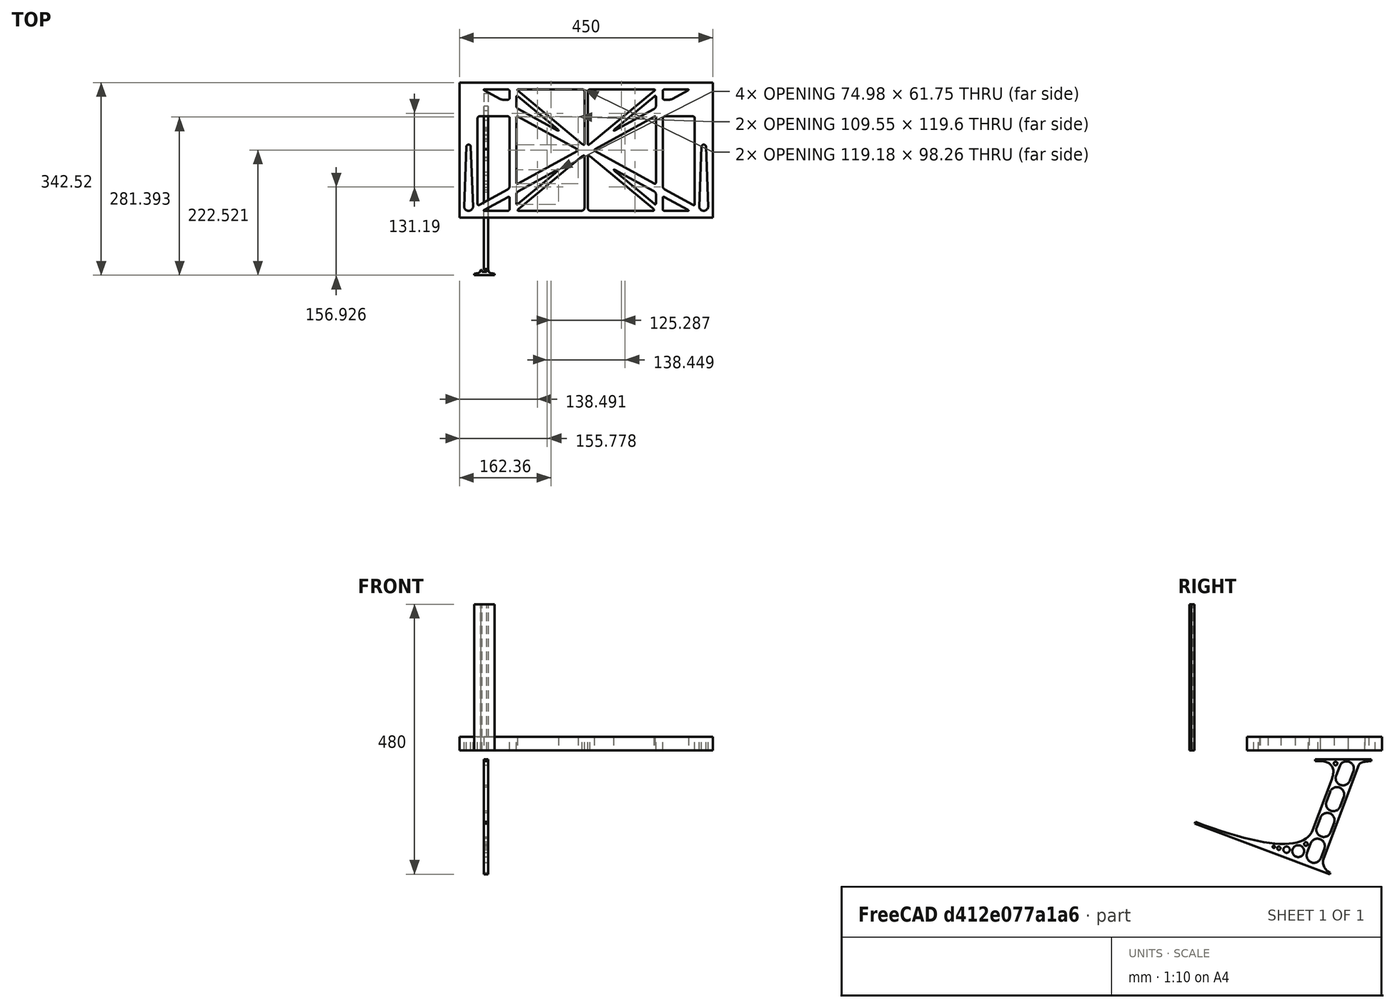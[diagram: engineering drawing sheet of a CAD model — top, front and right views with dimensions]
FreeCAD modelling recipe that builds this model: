
FCSTD DOCUMENT  (FreeCAD 0.19R0.19.2)
Label: laptopStand168FCStd
License: All rights reserved
LicenseURL: http://en.wikipedia.org/wiki/All_rights_reserved
objects: Sketcher::SketchObject×4, Part::Extrusion×3
note: 7 computed .brp shape members not serialized (recipe doc carries the construction recipe); baked Part::Feature solids carry a one-line shape summary decoded from their .brp

FEATURE [Sketcher::SketchObject] Sketch
  FullyConstrained = false
  sketch-geometry (349):
    g0: LineSegment StartX=-10.9272 StartY=-82.7794 StartZ=0 EndX=46.0728 EndY=-51.4823 EndZ=0
    g1: LineSegment StartX=-10.9272 StartY=76.4095 StartZ=0 EndX=-10.9272 EndY=-82.7794 EndZ=0
    g2: LineSegment StartX=46.0728 StartY=76.4095 StartZ=0 EndX=46.0728 EndY=-51.4823 EndZ=0
    g3: LineSegment StartX=-42.9272 StartY=136.221 StartZ=0 EndX=-42.9272 EndY=-103.779 EndZ=0
    g4: LineSegment StartX=407.073 StartY=136.221 StartZ=0 EndX=407.073 EndY=-103.779 EndZ=0
    g5: ArcOfCircle CenterX=-26.9272 CenterY=-83.7794 CenterZ=0 NormalX=0 NormalY=0 NormalZ=1 AngleXU=0 Radius=8 StartAngle=3.14159 EndAngle=6.28319
    g6: ArcOfCircle CenterX=391.073 CenterY=22.1087 CenterZ=0 NormalX=0 NormalY=0 NormalZ=1 AngleXU=0 Radius=8 StartAngle=-4.4e-15 EndAngle=3.14159
    g7: LineSegment StartX=399.073 StartY=22.1087 StartZ=0 EndX=399.073 EndY=-83.7794 EndZ=0
    g8: LineSegment StartX=383.073 StartY=22.1087 StartZ=0 EndX=383.073 EndY=-83.7794 EndZ=0
    g9: ArcOfCircle CenterX=391.073 CenterY=-83.7794 CenterZ=0 NormalX=0 NormalY=0 NormalZ=1 AngleXU=0 Radius=8 StartAngle=3.14159 EndAngle=6.28319
    g10: Circle CenterX=175.022 CenterY=27.0628 CenterZ=0 NormalX=0 NormalY=0 NormalZ=1 AngleXU=0 Radius=1
    g11: Circle CenterX=179.022 CenterY=24.8665 CenterZ=0 NormalX=0 NormalY=0 NormalZ=1 AngleXU=0 Radius=1
    g12: Circle CenterX=179.022 CenterY=27.0628 CenterZ=0 NormalX=0 NormalY=0 NormalZ=1 AngleXU=0 Radius=1
    g13: BSplineCurve PolesCount=3 KnotsCount=2 Degree=2 IsPeriodic=0
    g14: GeomPoint X=175.022 Y=27.0628 Z=0
    g15: GeomPoint X=179.022 Y=27.0628 Z=0
    g16: Circle CenterX=189.124 CenterY=27.0628 CenterZ=0 NormalX=0 NormalY=0 NormalZ=1 AngleXU=0 Radius=1
    g17: Circle CenterX=185.124 CenterY=24.8665 CenterZ=0 NormalX=0 NormalY=0 NormalZ=1 AngleXU=0 Radius=1
    g18: Circle CenterX=185.124 CenterY=27.0628 CenterZ=0 NormalX=0 NormalY=0 NormalZ=1 AngleXU=0 Radius=1
    g19: BSplineCurve PolesCount=3 KnotsCount=2 Degree=2 IsPeriodic=0
    g20: GeomPoint X=189.124 Y=27.0628 Z=0
    g21: GeomPoint X=185.124 Y=27.0628 Z=0
    g22: Circle CenterX=175.022 CenterY=5.37834 CenterZ=0 NormalX=0 NormalY=0 NormalZ=1 AngleXU=0 Radius=1
    g23: Circle CenterX=179.022 CenterY=7.57463 CenterZ=0 NormalX=0 NormalY=0 NormalZ=1 AngleXU=0 Radius=1
    g24: Circle CenterX=179.022 CenterY=5.34704 CenterZ=0 NormalX=0 NormalY=0 NormalZ=1 AngleXU=0 Radius=1
    g25: BSplineCurve PolesCount=3 KnotsCount=2 Degree=2 IsPeriodic=0
    g26: GeomPoint X=175.022 Y=5.37834 Z=0
    g27: GeomPoint X=179.022 Y=5.34704 Z=0
    g28: Circle CenterX=189.124 CenterY=5.37834 CenterZ=0 NormalX=0 NormalY=0 NormalZ=1 AngleXU=0 Radius=1
    g29: Circle CenterX=185.124 CenterY=7.57463 CenterZ=0 NormalX=0 NormalY=0 NormalZ=1 AngleXU=0 Radius=1
    g30: Circle CenterX=185.124 CenterY=5.34704 CenterZ=0 NormalX=0 NormalY=0 NormalZ=1 AngleXU=0 Radius=1
    g31: BSplineCurve PolesCount=3 KnotsCount=2 Degree=2 IsPeriodic=0
    g32: GeomPoint X=189.124 Y=5.37834 Z=0
    g33: GeomPoint X=185.124 Y=5.34704 Z=0
    g34: Circle CenterX=165.871 CenterY=18.1458 CenterZ=0 NormalX=0 NormalY=0 NormalZ=1 AngleXU=0 Radius=1
    g35: Circle CenterX=169.377 CenterY=16.2206 CenterZ=0 NormalX=0 NormalY=0 NormalZ=1 AngleXU=0 Radius=1
    g36: Circle CenterX=165.871 CenterY=14.2954 CenterZ=0 NormalX=0 NormalY=0 NormalZ=1 AngleXU=0 Radius=1
    g37: BSplineCurve PolesCount=3 KnotsCount=2 Degree=2 IsPeriodic=0
    g38: GeomPoint X=165.871 Y=18.1458 Z=0
    g39: GeomPoint X=165.871 Y=14.2954 Z=0
    g40: Circle CenterX=198.275 CenterY=18.1458 CenterZ=0 NormalX=0 NormalY=0 NormalZ=1 AngleXU=0 Radius=1
    g41: Circle CenterX=194.768 CenterY=16.2206 CenterZ=0 NormalX=0 NormalY=0 NormalZ=1 AngleXU=0 Radius=1
    g42: Circle CenterX=198.275 CenterY=14.2954 CenterZ=0 NormalX=0 NormalY=0 NormalZ=1 AngleXU=0 Radius=1
    g43: BSplineCurve PolesCount=3 KnotsCount=2 Degree=2 IsPeriodic=0
    g44: GeomPoint X=198.275 Y=18.1458 Z=0
    g45: GeomPoint X=198.275 Y=14.2954 Z=0
    g46: LineSegment StartX=407.073 StartY=-103.779 StartZ=0 EndX=-42.9272 EndY=-103.779 EndZ=0
    g47: LineSegment StartX=407.073 StartY=136.221 StartZ=0 EndX=-42.9272 EndY=136.221 EndZ=0
    g48: LineSegment StartX=46.0728 StartY=76.4095 StartZ=0 EndX=-10.9272 EndY=76.4095 EndZ=0
    g49: Circle CenterX=125.607 CenterY=54.1951 CenterZ=0 NormalX=0 NormalY=0 NormalZ=1 AngleXU=0 Radius=1
    g50: Circle CenterX=139.632 CenterY=46.4944 CenterZ=0 NormalX=0 NormalY=0 NormalZ=1 AngleXU=0 Radius=1
    g51: Circle CenterX=127.326 CenterY=56.7187 CenterZ=0 NormalX=0 NormalY=0 NormalZ=1 AngleXU=0 Radius=1
    g52: BSplineCurve PolesCount=3 KnotsCount=2 Degree=2 IsPeriodic=0
    g53: GeomPoint X=125.607 Y=54.1951 Z=0
    g54: GeomPoint X=127.326 Y=56.7187 Z=0
    g55: Circle CenterX=236.821 CenterY=56.7187 CenterZ=0 NormalX=0 NormalY=0 NormalZ=1 AngleXU=0 Radius=1
    g56: Circle CenterX=224.513 CenterY=46.4944 CenterZ=0 NormalX=0 NormalY=0 NormalZ=1 AngleXU=0 Radius=1
    g57: Circle CenterX=238.538 CenterY=54.1951 CenterZ=0 NormalX=0 NormalY=0 NormalZ=1 AngleXU=0 Radius=1
    g58: BSplineCurve PolesCount=3 KnotsCount=2 Degree=2 IsPeriodic=0
    g59: GeomPoint X=236.821 Y=56.7187 Z=0
    g60: GeomPoint X=238.538 Y=54.1951 Z=0
    g61: Circle CenterX=238.538 CenterY=-21.7539 CenterZ=0 NormalX=0 NormalY=0 NormalZ=1 AngleXU=0 Radius=1
    g62: Circle CenterX=224.513 CenterY=-14.0532 CenterZ=0 NormalX=0 NormalY=0 NormalZ=1 AngleXU=0 Radius=1
    g63: Circle CenterX=236.821 CenterY=-24.2775 CenterZ=0 NormalX=0 NormalY=0 NormalZ=1 AngleXU=0 Radius=1
    g64: BSplineCurve PolesCount=3 KnotsCount=2 Degree=2 IsPeriodic=0
    g65: GeomPoint X=238.538 Y=-21.7539 Z=0
    g66: GeomPoint X=236.821 Y=-24.2775 Z=0
    g67: Circle CenterX=125.607 CenterY=-21.7539 CenterZ=0 NormalX=0 NormalY=0 NormalZ=1 AngleXU=0 Radius=1
    g68: Circle CenterX=139.632 CenterY=-14.0532 CenterZ=0 NormalX=0 NormalY=0 NormalZ=1 AngleXU=0 Radius=1
    g69: Circle CenterX=127.325 CenterY=-24.2775 CenterZ=0 NormalX=0 NormalY=0 NormalZ=1 AngleXU=0 Radius=1
    g70: BSplineCurve PolesCount=3 KnotsCount=2 Degree=2 IsPeriodic=0
    g71: GeomPoint X=125.607 Y=-21.7539 Z=0
    g72: GeomPoint X=127.325 Y=-24.2775 Z=0
    g73: Circle CenterX=302.996 CenterY=111.695 CenterZ=0 NormalX=0 NormalY=0 NormalZ=1 AngleXU=0 Radius=1
    g74: Circle CenterX=306.073 CenterY=114.251 CenterZ=0 NormalX=0 NormalY=0 NormalZ=1 AngleXU=0 Radius=1
    g75: Circle CenterX=306.073 CenterY=110.251 CenterZ=0 NormalX=0 NormalY=0 NormalZ=1 AngleXU=0 Radius=1
    g76: BSplineCurve PolesCount=3 KnotsCount=2 Degree=2 IsPeriodic=0
    g77: GeomPoint X=302.996 Y=111.695 Z=0
    g78: GeomPoint X=306.073 Y=110.251 Z=0
    g79: Circle CenterX=306.073 CenterY=95.2763 CenterZ=0 NormalX=0 NormalY=0 NormalZ=1 AngleXU=0 Radius=1
    g80: Circle CenterX=306.073 CenterY=91.2763 CenterZ=0 NormalX=0 NormalY=0 NormalZ=1 AngleXU=0 Radius=1
    g81: Circle CenterX=302.567 CenterY=89.3511 CenterZ=0 NormalX=0 NormalY=0 NormalZ=1 AngleXU=0 Radius=1
    g82: BSplineCurve PolesCount=3 KnotsCount=2 Degree=2 IsPeriodic=0
    g83: GeomPoint X=306.073 Y=95.2763 Z=0
    g84: GeomPoint X=302.567 Y=89.3511 Z=0
    g85: LineSegment StartX=306.073 StartY=110.251 StartZ=0 EndX=306.073 EndY=95.2763 EndZ=0
    g86: LineSegment StartX=302.996 StartY=111.695 StartZ=0 EndX=236.821 EndY=56.7187 EndZ=0
    g87: LineSegment StartX=238.538 StartY=54.1951 StartZ=0 EndX=302.567 EndY=89.3511 EndZ=0
    g88: Circle CenterX=61.1496 CenterY=111.695 CenterZ=0 NormalX=0 NormalY=0 NormalZ=1 AngleXU=0 Radius=1
    g89: Circle CenterX=58.0728 CenterY=114.251 CenterZ=0 NormalX=0 NormalY=0 NormalZ=1 AngleXU=0 Radius=1
    g90: Circle CenterX=58.0728 CenterY=110.251 CenterZ=0 NormalX=0 NormalY=0 NormalZ=1 AngleXU=0 Radius=1
    g91: BSplineCurve PolesCount=3 KnotsCount=2 Degree=2 IsPeriodic=0
    g92: GeomPoint X=61.1496 Y=111.695 Z=0
    g93: GeomPoint X=58.0728 Y=110.251 Z=0
    g94: Circle CenterX=61.5791 CenterY=89.3511 CenterZ=0 NormalX=0 NormalY=0 NormalZ=1 AngleXU=0 Radius=1
    g95: Circle CenterX=58.0728 CenterY=91.2763 CenterZ=0 NormalX=0 NormalY=0 NormalZ=1 AngleXU=0 Radius=1
    g96: Circle CenterX=58.0728 CenterY=95.2763 CenterZ=0 NormalX=0 NormalY=0 NormalZ=1 AngleXU=0 Radius=1
    g97: BSplineCurve PolesCount=3 KnotsCount=2 Degree=2 IsPeriodic=0
    g98: GeomPoint X=61.5791 Y=89.3511 Z=0
    g99: GeomPoint X=58.0728 Y=95.2763 Z=0
    g100: LineSegment StartX=58.0728 StartY=110.251 StartZ=0 EndX=58.0728 EndY=95.2763 EndZ=0
    g101: LineSegment StartX=61.1496 StartY=111.695 StartZ=0 EndX=127.326 EndY=56.7187 EndZ=0
    g102: LineSegment StartX=125.607 StartY=54.1951 StartZ=0 EndX=61.5791 EndY=89.3511 EndZ=0
    g103: Circle CenterX=61.5791 CenterY=-56.9099 CenterZ=0 NormalX=0 NormalY=0 NormalZ=1 AngleXU=0 Radius=1
    g104: Circle CenterX=58.0728 CenterY=-58.8351 CenterZ=0 NormalX=0 NormalY=0 NormalZ=1 AngleXU=0 Radius=1
    g105: Circle CenterX=58.0728 CenterY=-62.8351 CenterZ=0 NormalX=0 NormalY=0 NormalZ=1 AngleXU=0 Radius=1
    g106: BSplineCurve PolesCount=3 KnotsCount=2 Degree=2 IsPeriodic=0
    g107: GeomPoint X=61.5791 Y=-56.9099 Z=0
    g108: GeomPoint X=58.0728 Y=-62.8351 Z=0
    g109: Circle CenterX=58.0728 CenterY=-77.8102 CenterZ=0 NormalX=0 NormalY=0 NormalZ=1 AngleXU=0 Radius=1
    g110: Circle CenterX=58.0728 CenterY=-81.8102 CenterZ=0 NormalX=0 NormalY=0 NormalZ=1 AngleXU=0 Radius=1
    g111: Circle CenterX=61.1496 CenterY=-79.2541 CenterZ=0 NormalX=0 NormalY=0 NormalZ=1 AngleXU=0 Radius=1
    g112: BSplineCurve PolesCount=3 KnotsCount=2 Degree=2 IsPeriodic=0
    g113: GeomPoint X=58.0728 Y=-77.8102 Z=0
    g114: GeomPoint X=61.1496 Y=-79.2541 Z=0
    g115: LineSegment StartX=58.0728 StartY=-62.8351 StartZ=0 EndX=58.0728 EndY=-77.8102 EndZ=0
    g116: LineSegment StartX=61.1496 StartY=-79.2541 StartZ=0 EndX=127.325 EndY=-24.2775 EndZ=0
    g117: LineSegment StartX=125.607 StartY=-21.7539 StartZ=0 EndX=61.5791 EndY=-56.9099 EndZ=0
    g118: Circle CenterX=302.567 CenterY=-56.9099 CenterZ=0 NormalX=0 NormalY=0 NormalZ=1 AngleXU=0 Radius=1
    g119: Circle CenterX=306.073 CenterY=-58.8351 CenterZ=0 NormalX=0 NormalY=0 NormalZ=1 AngleXU=0 Radius=1
    g120: Circle CenterX=306.073 CenterY=-62.8351 CenterZ=0 NormalX=0 NormalY=0 NormalZ=1 AngleXU=0 Radius=1
    g121: BSplineCurve PolesCount=3 KnotsCount=2 Degree=2 IsPeriodic=0
    g122: GeomPoint X=302.567 Y=-56.9099 Z=0
    g123: GeomPoint X=306.073 Y=-62.8351 Z=0
    g124: Circle CenterX=302.996 CenterY=-79.2541 CenterZ=0 NormalX=0 NormalY=0 NormalZ=1 AngleXU=0 Radius=1
    g125: Circle CenterX=306.073 CenterY=-81.8102 CenterZ=0 NormalX=0 NormalY=0 NormalZ=1 AngleXU=0 Radius=1
    g126: Circle CenterX=306.073 CenterY=-77.8102 CenterZ=0 NormalX=0 NormalY=0 NormalZ=1 AngleXU=0 Radius=1
    g127: BSplineCurve PolesCount=3 KnotsCount=2 Degree=2 IsPeriodic=0
    g128: GeomPoint X=302.996 Y=-79.2541 Z=0
    g129: GeomPoint X=306.073 Y=-77.8102 Z=0
    g130: LineSegment StartX=306.073 StartY=-62.8351 StartZ=0 EndX=306.073 EndY=-77.8102 EndZ=0
    g131: LineSegment StartX=302.996 StartY=-79.2541 StartZ=0 EndX=236.821 EndY=-24.2775 EndZ=0
    g132: LineSegment StartX=238.538 StartY=-21.7539 StartZ=0 EndX=302.567 EndY=-56.9099 EndZ=0
    g133: Circle CenterX=61.6457 CenterY=-88.8112 CenterZ=0 NormalX=0 NormalY=0 NormalZ=1 AngleXU=0 Radius=1
    g134: Circle CenterX=58.0728 CenterY=-91.7794 CenterZ=0 NormalX=0 NormalY=0 NormalZ=1 AngleXU=0 Radius=1
    g135: Circle CenterX=63.9135 CenterY=-91.7794 CenterZ=0 NormalX=0 NormalY=0 NormalZ=1 AngleXU=0 Radius=1
    g136: BSplineCurve PolesCount=3 KnotsCount=2 Degree=2 IsPeriodic=0
    g137: GeomPoint X=61.6457 Y=-88.8112 Z=0
    g138: GeomPoint X=63.9135 Y=-91.7794 Z=0
    g139: Circle CenterX=179.022 CenterY=-85.8163 CenterZ=0 NormalX=0 NormalY=0 NormalZ=1 AngleXU=0 Radius=1
    g140: Circle CenterX=179.022 CenterY=-91.7794 CenterZ=0 NormalX=0 NormalY=0 NormalZ=1 AngleXU=0 Radius=1
    g141: Circle CenterX=171.895 CenterY=-91.7794 CenterZ=0 NormalX=0 NormalY=0 NormalZ=1 AngleXU=0 Radius=1
    g142: BSplineCurve PolesCount=3 KnotsCount=2 Degree=2 IsPeriodic=0
    g143: GeomPoint X=179.022 Y=-85.8163 Z=0
    g144: GeomPoint X=171.895 Y=-91.7794 Z=0
    g145: Circle CenterX=185.124 CenterY=-86.2028 CenterZ=0 NormalX=0 NormalY=0 NormalZ=1 AngleXU=0 Radius=1
    g146: Circle CenterX=185.124 CenterY=-91.7794 CenterZ=0 NormalX=0 NormalY=0 NormalZ=1 AngleXU=0 Radius=1
    g147: Circle CenterX=191.747 CenterY=-91.7794 CenterZ=0 NormalX=0 NormalY=0 NormalZ=1 AngleXU=0 Radius=1
    g148: BSplineCurve PolesCount=3 KnotsCount=2 Degree=2 IsPeriodic=0
    g149: GeomPoint X=185.124 Y=-86.2028 Z=0
    g150: GeomPoint X=191.747 Y=-91.7794 Z=0
    g151: Circle CenterX=299.888 CenterY=-86.6413 CenterZ=0 NormalX=0 NormalY=0 NormalZ=1 AngleXU=0 Radius=1
    g152: Circle CenterX=306.073 CenterY=-91.7794 CenterZ=0 NormalX=0 NormalY=0 NormalZ=1 AngleXU=0 Radius=1
    g153: Circle CenterX=298.776 CenterY=-91.7794 CenterZ=0 NormalX=0 NormalY=0 NormalZ=1 AngleXU=0 Radius=1
    g154: BSplineCurve PolesCount=3 KnotsCount=2 Degree=2 IsPeriodic=0
    g155: GeomPoint X=299.888 Y=-86.6413 Z=0
    g156: GeomPoint X=298.776 Y=-91.7794 Z=0
    g157: LineSegment StartX=189.124 StartY=5.37834 StartZ=0 EndX=299.888 EndY=-86.6413 EndZ=0
    g158: LineSegment StartX=298.776 StartY=-91.7794 StartZ=0 EndX=191.747 EndY=-91.7794 EndZ=0
    g159: LineSegment StartX=185.124 StartY=-86.2028 StartZ=0 EndX=185.124 EndY=5.34704 EndZ=0
    g160: LineSegment StartX=179.022 StartY=5.34704 StartZ=0 EndX=179.022 EndY=-85.8163 EndZ=0
    g161: LineSegment StartX=171.895 StartY=-91.7794 StartZ=0 EndX=63.9135 EndY=-91.7794 EndZ=0
    g162: LineSegment StartX=61.6457 StartY=-88.8112 StartZ=0 EndX=175.022 EndY=5.37834 EndZ=0
    g163: Circle CenterX=302.073 CenterY=124.221 CenterZ=0 NormalX=0 NormalY=0 NormalZ=1 AngleXU=0 Radius=1
    g164: Circle CenterX=306.073 CenterY=124.221 CenterZ=0 NormalX=0 NormalY=0 NormalZ=1 AngleXU=0 Radius=1
    g165: Circle CenterX=302.996 CenterY=121.665 CenterZ=0 NormalX=0 NormalY=0 NormalZ=1 AngleXU=0 Radius=1
    g166: BSplineCurve PolesCount=3 KnotsCount=2 Degree=2 IsPeriodic=0
    g167: GeomPoint X=302.073 Y=124.221 Z=0
    g168: GeomPoint X=302.996 Y=121.665 Z=0
    g169: Circle CenterX=189.124 CenterY=124.221 CenterZ=0 NormalX=0 NormalY=0 NormalZ=1 AngleXU=0 Radius=1
    g170: Circle CenterX=185.124 CenterY=124.221 CenterZ=0 NormalX=0 NormalY=0 NormalZ=1 AngleXU=0 Radius=1
    g171: Circle CenterX=185.124 CenterY=120.221 CenterZ=0 NormalX=0 NormalY=0 NormalZ=1 AngleXU=0 Radius=1
    g172: BSplineCurve PolesCount=3 KnotsCount=2 Degree=2 IsPeriodic=0
    g173: GeomPoint X=189.124 Y=124.221 Z=0
    g174: GeomPoint X=185.124 Y=120.221 Z=0
    g175: Circle CenterX=175.022 CenterY=124.221 CenterZ=0 NormalX=0 NormalY=0 NormalZ=1 AngleXU=0 Radius=1
    g176: Circle CenterX=179.022 CenterY=124.221 CenterZ=0 NormalX=0 NormalY=0 NormalZ=1 AngleXU=0 Radius=1
    g177: Circle CenterX=179.022 CenterY=120.221 CenterZ=0 NormalX=0 NormalY=0 NormalZ=1 AngleXU=0 Radius=1
    g178: BSplineCurve PolesCount=3 KnotsCount=2 Degree=2 IsPeriodic=0
    g179: GeomPoint X=175.022 Y=124.221 Z=0
    g180: GeomPoint X=179.022 Y=120.221 Z=0
    g181: Circle CenterX=62.0728 CenterY=124.221 CenterZ=0 NormalX=0 NormalY=0 NormalZ=1 AngleXU=0 Radius=1
    g182: Circle CenterX=58.0728 CenterY=124.221 CenterZ=0 NormalX=0 NormalY=0 NormalZ=1 AngleXU=0 Radius=1
    g183: Circle CenterX=61.1496 CenterY=121.665 CenterZ=0 NormalX=0 NormalY=0 NormalZ=1 AngleXU=0 Radius=1
    g184: BSplineCurve PolesCount=3 KnotsCount=2 Degree=2 IsPeriodic=0
    g185: GeomPoint X=62.0728 Y=124.221 Z=0
    g186: GeomPoint X=61.1496 Y=121.665 Z=0
    g187: LineSegment StartX=62.0728 StartY=124.221 StartZ=0 EndX=175.022 EndY=124.221 EndZ=0
    g188: LineSegment StartX=179.022 StartY=120.221 StartZ=0 EndX=179.022 EndY=27.0628 EndZ=0
    g189: LineSegment StartX=185.124 StartY=27.0628 StartZ=0 EndX=185.124 EndY=120.221 EndZ=0
    g190: LineSegment StartX=189.124 StartY=124.221 StartZ=0 EndX=302.073 EndY=124.221 EndZ=0
    g191: LineSegment StartX=302.996 StartY=121.665 StartZ=0 EndX=189.124 EndY=27.0628 EndZ=0
    g192: LineSegment StartX=175.022 StartY=27.0628 StartZ=0 EndX=61.1496 EndY=121.665 EndZ=0
    g193: Circle CenterX=61.5791 CenterY=75.4095 CenterZ=0 NormalX=0 NormalY=0 NormalZ=1 AngleXU=0 Radius=1
    g194: Circle CenterX=58.0728 CenterY=77.3346 CenterZ=0 NormalX=0 NormalY=0 NormalZ=1 AngleXU=0 Radius=1
    g195: Circle CenterX=58.0728 CenterY=73.3346 CenterZ=0 NormalX=0 NormalY=0 NormalZ=1 AngleXU=0 Radius=1
    g196: BSplineCurve PolesCount=3 KnotsCount=2 Degree=2 IsPeriodic=0
    g197: GeomPoint X=61.5791 Y=75.4095 Z=0
    g198: GeomPoint X=58.0728 Y=73.3346 Z=0
    g199: Circle CenterX=58.0728 CenterY=-40.8935 CenterZ=0 NormalX=0 NormalY=0 NormalZ=1 AngleXU=0 Radius=1
    g200: Circle CenterX=58.0728 CenterY=-44.8935 CenterZ=0 NormalX=0 NormalY=0 NormalZ=1 AngleXU=0 Radius=1
    g201: Circle CenterX=61.5791 CenterY=-42.9683 CenterZ=0 NormalX=0 NormalY=0 NormalZ=1 AngleXU=0 Radius=1
    g202: BSplineCurve PolesCount=3 KnotsCount=2 Degree=2 IsPeriodic=0
    g203: GeomPoint X=58.0728 Y=-40.8935 Z=0
    g204: GeomPoint X=61.5791 Y=-42.9683 Z=0
    g205: LineSegment StartX=61.5791 StartY=-42.9683 StartZ=0 EndX=165.871 EndY=14.2954 EndZ=0
    g206: LineSegment StartX=165.871 StartY=18.1458 StartZ=0 EndX=61.5791 EndY=75.4095 EndZ=0
    g207: LineSegment StartX=58.0728 StartY=73.3346 StartZ=0 EndX=58.0728 EndY=-40.8935 EndZ=0
    g208: Circle CenterX=302.567 CenterY=-42.9683 CenterZ=0 NormalX=0 NormalY=0 NormalZ=1 AngleXU=0 Radius=1
    g209: Circle CenterX=306.073 CenterY=-44.8935 CenterZ=0 NormalX=0 NormalY=0 NormalZ=1 AngleXU=0 Radius=1
    g210: Circle CenterX=306.073 CenterY=-40.8935 CenterZ=0 NormalX=0 NormalY=0 NormalZ=1 AngleXU=0 Radius=1
    g211: BSplineCurve PolesCount=3 KnotsCount=2 Degree=2 IsPeriodic=0
    g212: GeomPoint X=302.567 Y=-42.9683 Z=0
    g213: GeomPoint X=306.073 Y=-40.8935 Z=0
    g214: Circle CenterX=306.073 CenterY=73.3346 CenterZ=0 NormalX=0 NormalY=0 NormalZ=1 AngleXU=0 Radius=1
    g215: Circle CenterX=306.073 CenterY=77.3346 CenterZ=0 NormalX=0 NormalY=0 NormalZ=1 AngleXU=0 Radius=1
    g216: Circle CenterX=302.567 CenterY=75.4095 CenterZ=0 NormalX=0 NormalY=0 NormalZ=1 AngleXU=0 Radius=1
    g217: BSplineCurve PolesCount=3 KnotsCount=2 Degree=2 IsPeriodic=0
    g218: GeomPoint X=306.073 Y=73.3346 Z=0
    g219: GeomPoint X=302.567 Y=75.4095 Z=0
    g220: LineSegment StartX=302.567 StartY=-42.9683 StartZ=0 EndX=198.275 EndY=14.2954 EndZ=0
    g221: LineSegment StartX=198.275 StartY=18.1458 StartZ=0 EndX=302.567 EndY=75.4095 EndZ=0
    g222: LineSegment StartX=306.073 StartY=73.3346 StartZ=0 EndX=306.073 EndY=-40.8935 EndZ=0
    g223: LineSegment StartX=322.073 StartY=105.865 StartZ=0 EndX=328.643 EndY=105.865 EndZ=0
    g224: LineSegment StartX=318.073 StartY=120.221 StartZ=0 EndX=318.073 EndY=109.865 EndZ=0
    g225: LineSegment StartX=336.157 StartY=107.779 StartZ=0 EndX=362.567 EndY=122.294 EndZ=0
    g226: Circle CenterX=362.073 CenterY=124.221 CenterZ=0 NormalX=0 NormalY=0 NormalZ=1 AngleXU=0 Radius=1
    g227: Circle CenterX=366.073 CenterY=124.221 CenterZ=0 NormalX=0 NormalY=0 NormalZ=1 AngleXU=0 Radius=1
    g228: Circle CenterX=362.567 CenterY=122.294 CenterZ=0 NormalX=0 NormalY=0 NormalZ=1 AngleXU=0 Radius=1
    g229: BSplineCurve PolesCount=3 KnotsCount=2 Degree=2 IsPeriodic=0
    g230: GeomPoint X=362.073 Y=124.221 Z=0
    g231: GeomPoint X=362.567 Y=122.294 Z=0
    g232: Circle CenterX=322.073 CenterY=124.221 CenterZ=0 NormalX=0 NormalY=0 NormalZ=1 AngleXU=0 Radius=1
    g233: Circle CenterX=318.073 CenterY=124.221 CenterZ=0 NormalX=0 NormalY=0 NormalZ=1 AngleXU=0 Radius=1
    g234: Circle CenterX=318.073 CenterY=120.221 CenterZ=0 NormalX=0 NormalY=0 NormalZ=1 AngleXU=0 Radius=1
    g235: BSplineCurve PolesCount=3 KnotsCount=2 Degree=2 IsPeriodic=0
    g236: GeomPoint X=322.073 Y=124.221 Z=0
    g237: GeomPoint X=318.073 Y=120.221 Z=0
    g238: Circle CenterX=322.073 CenterY=105.865 CenterZ=0 NormalX=0 NormalY=0 NormalZ=1 AngleXU=0 Radius=1
    g239: Circle CenterX=318.073 CenterY=105.865 CenterZ=0 NormalX=0 NormalY=0 NormalZ=1 AngleXU=0 Radius=1
    g240: Circle CenterX=318.073 CenterY=109.865 CenterZ=0 NormalX=0 NormalY=0 NormalZ=1 AngleXU=0 Radius=1
    g241: BSplineCurve PolesCount=3 KnotsCount=2 Degree=2 IsPeriodic=0
    g242: GeomPoint X=322.073 Y=105.865 Z=0
    g243: GeomPoint X=318.073 Y=109.865 Z=0
    g244: Circle CenterX=336.157 CenterY=107.779 CenterZ=0 NormalX=0 NormalY=0 NormalZ=1 AngleXU=0 Radius=1
    g245: Circle CenterX=332.651 CenterY=105.853 CenterZ=0 NormalX=0 NormalY=0 NormalZ=1 AngleXU=0 Radius=1
    g246: Circle CenterX=328.643 CenterY=105.865 CenterZ=0 NormalX=0 NormalY=0 NormalZ=1 AngleXU=0 Radius=1
    g247: BSplineCurve PolesCount=3 KnotsCount=2 Degree=2 IsPeriodic=0
    g248: GeomPoint X=336.157 Y=107.779 Z=0
    g249: GeomPoint X=328.643 Y=105.865 Z=0
    g250: LineSegment StartX=322.073 StartY=124.221 StartZ=0 EndX=362.073 EndY=124.221 EndZ=0
    g251: Circle CenterX=371.567 CenterY=-80.8644 CenterZ=0 NormalX=0 NormalY=0 NormalZ=1 AngleXU=0 Radius=1
    g252: Circle CenterX=375.073 CenterY=-82.7896 CenterZ=0 NormalX=0 NormalY=0 NormalZ=1 AngleXU=0 Radius=1
    g253: Circle CenterX=375.073 CenterY=-78.7896 CenterZ=0 NormalX=0 NormalY=0 NormalZ=1 AngleXU=0 Radius=1
    g254: BSplineCurve PolesCount=3 KnotsCount=2 Degree=2 IsPeriodic=0
    g255: GeomPoint X=371.567 Y=-80.8644 Z=0
    g256: GeomPoint X=375.073 Y=-78.7896 Z=0
    g257: Circle CenterX=321.579 CenterY=-53.4075 CenterZ=0 NormalX=0 NormalY=0 NormalZ=1 AngleXU=0 Radius=1
    g258: Circle CenterX=318.073 CenterY=-51.4823 CenterZ=0 NormalX=0 NormalY=0 NormalZ=1 AngleXU=0 Radius=1
    g259: Circle CenterX=318.073 CenterY=-47.4805 CenterZ=0 NormalX=0 NormalY=0 NormalZ=1 AngleXU=0 Radius=1
    g260: BSplineCurve PolesCount=3 KnotsCount=2 Degree=2 IsPeriodic=0
    g261: GeomPoint X=321.579 Y=-53.4075 Z=0
    g262: GeomPoint X=318.073 Y=-47.4805 Z=0
    g263: LineSegment StartX=371.567 StartY=-80.8644 StartZ=0 EndX=321.579 EndY=-53.4075 EndZ=0
    g264: Circle CenterX=321.579 CenterY=-67.3492 CenterZ=0 NormalX=0 NormalY=0 NormalZ=1 AngleXU=0 Radius=1
    g265: Circle CenterX=318.073 CenterY=-65.424 CenterZ=0 NormalX=0 NormalY=0 NormalZ=1 AngleXU=0 Radius=1
    g266: Circle CenterX=318.073 CenterY=-69.424 CenterZ=0 NormalX=0 NormalY=0 NormalZ=1 AngleXU=0 Radius=1
    g267: BSplineCurve PolesCount=3 KnotsCount=2 Degree=2 IsPeriodic=0
    g268: GeomPoint X=321.579 Y=-67.3492 Z=0
    g269: GeomPoint X=318.073 Y=-69.424 Z=0
    g270: Circle CenterX=362.567 CenterY=-89.8542 CenterZ=0 NormalX=0 NormalY=0 NormalZ=1 AngleXU=0 Radius=1
    g271: Circle CenterX=366.073 CenterY=-91.7794 CenterZ=0 NormalX=0 NormalY=0 NormalZ=1 AngleXU=0 Radius=1
    g272: Circle CenterX=362.073 CenterY=-91.7794 CenterZ=0 NormalX=0 NormalY=0 NormalZ=1 AngleXU=0 Radius=1
    g273: BSplineCurve PolesCount=3 KnotsCount=2 Degree=2 IsPeriodic=0
    g274: GeomPoint X=362.567 Y=-89.8542 Z=0
    g275: GeomPoint X=362.073 Y=-91.7794 Z=0
    g276: Circle CenterX=322.073 CenterY=-91.7794 CenterZ=0 NormalX=0 NormalY=0 NormalZ=1 AngleXU=0 Radius=1
    g277: Circle CenterX=318.073 CenterY=-91.7794 CenterZ=0 NormalX=0 NormalY=0 NormalZ=1 AngleXU=0 Radius=1
    g278: Circle CenterX=318.073 CenterY=-87.7794 CenterZ=0 NormalX=0 NormalY=0 NormalZ=1 AngleXU=0 Radius=1
    g279: BSplineCurve PolesCount=3 KnotsCount=2 Degree=2 IsPeriodic=0
    g280: GeomPoint X=322.073 Y=-91.7794 Z=0
    g281: GeomPoint X=318.073 Y=-87.7794 Z=0
    g282: LineSegment StartX=362.567 StartY=-89.8542 StartZ=0 EndX=321.579 EndY=-67.3492 EndZ=0
    g283: LineSegment StartX=318.073 StartY=-69.424 StartZ=0 EndX=318.073 EndY=-87.7794 EndZ=0
    g284: LineSegment StartX=322.073 StartY=-91.7794 StartZ=0 EndX=362.073 EndY=-91.7794 EndZ=0
    g285: Circle CenterX=2.07281 CenterY=124.221 CenterZ=0 NormalX=0 NormalY=0 NormalZ=1 AngleXU=0 Radius=1
    g286: Circle CenterX=1.57905 CenterY=122.295 CenterZ=0 NormalX=0 NormalY=0 NormalZ=1 AngleXU=0 Radius=1
    g287: BSplineCurve PolesCount=3 KnotsCount=2 Degree=2 IsPeriodic=0
    g288: GeomPoint X=2.07281 Y=124.221 Z=0
    g289: GeomPoint X=1.57905 Y=122.295 Z=0
    g290: Circle CenterX=42.0728 CenterY=124.221 CenterZ=0 NormalX=0 NormalY=0 NormalZ=1 AngleXU=0 Radius=1
    g291: Circle CenterX=46.0728 CenterY=124.221 CenterZ=0 NormalX=0 NormalY=0 NormalZ=1 AngleXU=0 Radius=1
    g292: Circle CenterX=46.0728 CenterY=120.221 CenterZ=0 NormalX=0 NormalY=0 NormalZ=1 AngleXU=0 Radius=1
    g293: BSplineCurve PolesCount=3 KnotsCount=2 Degree=2 IsPeriodic=0
    g294: GeomPoint X=42.0728 Y=124.221 Z=0
    g295: GeomPoint X=46.0728 Y=120.221 Z=0
    g296: Circle CenterX=46.0728 CenterY=109.865 CenterZ=0 NormalX=0 NormalY=0 NormalZ=1 AngleXU=0 Radius=1
    g297: Circle CenterX=46.0728 CenterY=105.865 CenterZ=0 NormalX=0 NormalY=0 NormalZ=1 AngleXU=0 Radius=1
    g298: Circle CenterX=42.0728 CenterY=105.865 CenterZ=0 NormalX=0 NormalY=0 NormalZ=1 AngleXU=0 Radius=1
    g299: BSplineCurve PolesCount=3 KnotsCount=2 Degree=2 IsPeriodic=0
    g300: GeomPoint X=46.0728 Y=109.865 Z=0
    g301: GeomPoint X=42.0728 Y=105.865 Z=0
    g302: Circle CenterX=35.5028 CenterY=105.865 CenterZ=0 NormalX=0 NormalY=0 NormalZ=1 AngleXU=0 Radius=1
    g303: Circle CenterX=31.5028 CenterY=105.865 CenterZ=0 NormalX=0 NormalY=0 NormalZ=1 AngleXU=0 Radius=1
    g304: Circle CenterX=27.9965 CenterY=107.79 CenterZ=0 NormalX=0 NormalY=0 NormalZ=1 AngleXU=0 Radius=1
    g305: BSplineCurve PolesCount=3 KnotsCount=2 Degree=2 IsPeriodic=0
    g306: GeomPoint X=35.5028 Y=105.865 Z=0
    g307: GeomPoint X=27.9965 Y=107.79 Z=0
    g308: LineSegment StartX=2.07281 StartY=124.221 StartZ=0 EndX=42.0728 EndY=124.221 EndZ=0
    g309: LineSegment StartX=46.0728 StartY=120.221 StartZ=0 EndX=46.0728 EndY=109.865 EndZ=0
    g310: LineSegment StartX=42.0728 StartY=105.865 StartZ=0 EndX=35.5028 EndY=105.865 EndZ=0
    g311: LineSegment StartX=27.9965 StartY=107.79 StartZ=0 EndX=1.57905 EndY=122.295 EndZ=0
    g312: Circle CenterX=42.5666 CenterY=-67.3492 CenterZ=0 NormalX=0 NormalY=0 NormalZ=1 AngleXU=0 Radius=1
    g313: Circle CenterX=46.0728 CenterY=-65.424 CenterZ=0 NormalX=0 NormalY=0 NormalZ=1 AngleXU=0 Radius=1
    g314: Circle CenterX=46.0728 CenterY=-69.424 CenterZ=0 NormalX=0 NormalY=0 NormalZ=1 AngleXU=0 Radius=1
    g315: BSplineCurve PolesCount=3 KnotsCount=2 Degree=2 IsPeriodic=0
    g316: GeomPoint X=42.5666 Y=-67.3492 Z=0
    g317: GeomPoint X=46.0728 Y=-69.424 Z=0
    g318: Circle CenterX=46.0728 CenterY=-87.7794 CenterZ=0 NormalX=0 NormalY=0 NormalZ=1 AngleXU=0 Radius=1
    g319: Circle CenterX=46.0728 CenterY=-91.7794 CenterZ=0 NormalX=0 NormalY=0 NormalZ=1 AngleXU=0 Radius=1
    g320: Circle CenterX=42.0728 CenterY=-91.7794 CenterZ=0 NormalX=0 NormalY=0 NormalZ=1 AngleXU=0 Radius=1
    g321: BSplineCurve PolesCount=3 KnotsCount=2 Degree=2 IsPeriodic=0
    g322: GeomPoint X=46.0728 Y=-87.7794 Z=0
    g323: GeomPoint X=42.0728 Y=-91.7794 Z=0
    g324: Circle CenterX=2.07281 CenterY=-91.7794 CenterZ=0 NormalX=0 NormalY=0 NormalZ=1 AngleXU=0 Radius=1
    g325: Circle CenterX=-1.92719 CenterY=-91.7794 CenterZ=0 NormalX=0 NormalY=0 NormalZ=1 AngleXU=0 Radius=1
    g326: Circle CenterX=1.57905 CenterY=-89.8542 CenterZ=0 NormalX=0 NormalY=0 NormalZ=1 AngleXU=0 Radius=1
    g327: BSplineCurve PolesCount=3 KnotsCount=2 Degree=2 IsPeriodic=0
    g328: GeomPoint X=2.07281 Y=-91.7794 Z=0
    g329: GeomPoint X=1.57905 Y=-89.8542 Z=0
    g330: LineSegment StartX=2.07281 StartY=-91.7794 StartZ=0 EndX=42.0728 EndY=-91.7794 EndZ=0
    g331: LineSegment StartX=46.0728 StartY=-87.7794 StartZ=0 EndX=46.0728 EndY=-69.424 EndZ=0
    g332: LineSegment StartX=42.5666 StartY=-67.3492 StartZ=0 EndX=1.57905 EndY=-89.8542 EndZ=0
    g333: Circle CenterX=322.073 CenterY=76.4095 CenterZ=0 NormalX=0 NormalY=0 NormalZ=1 AngleXU=0 Radius=4
    g334: BSplineCurve PolesCount=3 KnotsCount=2 Degree=2 IsPeriodic=0
    g335: GeomPoint X=318.073 Y=72.4095 Z=0
    g336: GeomPoint X=322.073 Y=76.4095 Z=0
    g337: Circle CenterX=375.073 CenterY=72.4095 CenterZ=0 NormalX=0 NormalY=0 NormalZ=1 AngleXU=0 Radius=1
    g338: Circle CenterX=375.073 CenterY=76.4095 CenterZ=0 NormalX=0 NormalY=0 NormalZ=1 AngleXU=0 Radius=1
    g339: Circle CenterX=371.073 CenterY=76.4095 CenterZ=0 NormalX=0 NormalY=0 NormalZ=1 AngleXU=0 Radius=1
    g340: BSplineCurve PolesCount=3 KnotsCount=2 Degree=2 IsPeriodic=0
    g341: GeomPoint X=375.073 Y=72.4095 Z=0
    g342: GeomPoint X=371.073 Y=76.4095 Z=0
    g343: LineSegment StartX=322.073 StartY=76.4095 StartZ=0 EndX=371.073 EndY=76.4095 EndZ=0
    g344: LineSegment StartX=318.073 StartY=72.4095 StartZ=0 EndX=318.073 EndY=-47.4805 EndZ=0
    g345: LineSegment StartX=375.073 StartY=72.4095 StartZ=0 EndX=375.073 EndY=-78.7896 EndZ=0
    g346: ArcOfCircle CenterX=-26.9272 CenterY=22.1087 CenterZ=0 NormalX=0 NormalY=0 NormalZ=1 AngleXU=0 Radius=4 StartAngle=5e-16 EndAngle=3.14159
    g347: LineSegment StartX=-30.9272 StartY=22.1087 StartZ=0 EndX=-34.9272 EndY=-83.7794 EndZ=0
    g348: LineSegment StartX=-18.9272 StartY=-83.7794 StartZ=0 EndX=-22.9272 EndY=22.1087 EndZ=0
  constraints (572):
    c: Coincident(g0,g2)
    c: Block(g0)
    c: Block(g1)
    c: Vertical(g3)
    c: Vertical(g4)
    c: Block(g4)
    c: Block(g3)
    c: Tangent(g6,g7) = 1.5708
    c: Tangent(g7,g9) = 1.5708
    c: Equal(g6,g9)
    c: Coincident(g8,g6)
    c: Coincident(g8,g9)
    c: Block(g7)
    c: Block(g8)
    c: Weight(g10) = 1
    c: Equal(g10,g11)
    c: Equal(g10,g12)
    c: InternalAlignment(g10,g13)
    c: InternalAlignment(g11,g13)
    c: InternalAlignment(g12,g13)
    c: InternalAlignment(g14,g13)
    c: InternalAlignment(g15,g13)
    c: Weight(g16) = 1
    c: Equal(g16,g17)
    c: Equal(g16,g18)
    c: InternalAlignment(g16,g19)
    c: InternalAlignment(g17,g19)
    c: InternalAlignment(g18,g19)
    c: InternalAlignment(g20,g19)
    c: InternalAlignment(g21,g19)
    c: Block(g19)
    c: Block(g13)
    c: Weight(g22) = 1
    c: Equal(g22,g23)
    c: Equal(g22,g24)
    c: InternalAlignment(g22,g25)
    c: InternalAlignment(g23,g25)
    c: InternalAlignment(g24,g25)
    c: InternalAlignment(g26,g25)
    c: InternalAlignment(g27,g25)
    c: Weight(g28) = 1
    c: Equal(g28,g29)
    c: Equal(g28,g30)
    c: InternalAlignment(g28,g31)
    c: InternalAlignment(g29,g31)
    c: InternalAlignment(g30,g31)
    c: InternalAlignment(g32,g31)
    c: InternalAlignment(g33,g31)
    c: Block(g31)
    c: Block(g25)
    c: Weight(g34) = 1
    c: Equal(g34,g35)
    c: Equal(g34,g36)
    c: InternalAlignment(g34,g37)
    c: InternalAlignment(g35,g37)
    c: InternalAlignment(g36,g37)
    c: InternalAlignment(g38,g37)
    c: InternalAlignment(g39,g37)
    c: Weight(g40) = 1
    c: Equal(g40,g41)
    c: Equal(g40,g42)
    c: InternalAlignment(g40,g43)
    c: InternalAlignment(g41,g43)
    c: InternalAlignment(g42,g43)
    c: InternalAlignment(g44,g43)
    c: InternalAlignment(g45,g43)
    c: Block(g37)
    c: Block(g43)
    c: Coincident(g46,g4)
    c: Coincident(g46,g3)
    c: Horizontal(g46)
    c: Distance(g46) = 450
    c: Coincident(g47,g4)
    c: Coincident(g47,g3)
    c: Horizontal(g47)
    c: Horizontal(g48)
    c: Coincident(g2,g48)
    c: Block(g48)
    c: Coincident(g1,g48)
    c: Weight(g49) = 1
    c: Equal(g49,g50)
    c: Equal(g49,g51)
    c: InternalAlignment(g49,g52)
    c: InternalAlignment(g50,g52)
    c: InternalAlignment(g51,g52)
    c: InternalAlignment(g53,g52)
    c: InternalAlignment(g54,g52)
    c: Block(g52)
    c: Weight(g55) = 1
    c: Equal(g55,g56)
    c: Equal(g55,g57)
    c: InternalAlignment(g55,g58)
    c: InternalAlignment(g56,g58)
    c: InternalAlignment(g57,g58)
    c: InternalAlignment(g59,g58)
    c: InternalAlignment(g60,g58)
    c: Block(g58)
    c: Weight(g61) = 1
    c: Equal(g61,g62)
    c: Equal(g61,g63)
    c: InternalAlignment(g61,g64)
    c: InternalAlignment(g62,g64)
    c: InternalAlignment(g63,g64)
    c: InternalAlignment(g65,g64)
    c: InternalAlignment(g66,g64)
    c: Block(g64)
    c: Weight(g67) = 1
    c: Equal(g67,g68)
    c: Equal(g67,g69)
    c: InternalAlignment(g67,g70)
    c: InternalAlignment(g68,g70)
    c: InternalAlignment(g69,g70)
    c: InternalAlignment(g71,g70)
    c: InternalAlignment(g72,g70)
    c: Block(g70)
    c: Weight(g73) = 1
    c: Equal(g73,g74)
    c: Equal(g73,g75)
    c: InternalAlignment(g73,g76)
    c: InternalAlignment(g74,g76)
    c: InternalAlignment(g75,g76)
    c: InternalAlignment(g77,g76)
    c: InternalAlignment(g78,g76)
    c: Weight(g79) = 1
    c: Equal(g79,g80)
    c: Equal(g79,g81)
    c: InternalAlignment(g79,g82)
    c: InternalAlignment(g80,g82)
    c: InternalAlignment(g81,g82)
    c: InternalAlignment(g83,g82)
    c: InternalAlignment(g84,g82)
    c: Block(g76)
    c: Block(g82)
    c: Coincident(g85,g76)
    c: Coincident(g85,g82)
    c: Vertical(g85)
    c: Coincident(g86,g76)
    c: Coincident(g86,g58)
    c: Coincident(g87,g58)
    c: Coincident(g87,g82)
    c: Weight(g88) = 1
    c: Equal(g88,g89)
    c: Equal(g88,g90)
    c: InternalAlignment(g88,g91)
    c: InternalAlignment(g89,g91)
    c: InternalAlignment(g90,g91)
    c: InternalAlignment(g92,g91)
    c: InternalAlignment(g93,g91)
    c: Weight(g94) = 1
    c: Equal(g94,g95)
    c: Equal(g94,g96)
    c: InternalAlignment(g94,g97)
    c: InternalAlignment(g95,g97)
    c: InternalAlignment(g96,g97)
    c: InternalAlignment(g98,g97)
    c: InternalAlignment(g99,g97)
    c: Block(g91)
    c: Block(g97)
    c: Coincident(g100,g91)
    c: Coincident(g100,g97)
    c: Vertical(g100)
    c: Coincident(g101,g91)
    c: Coincident(g101,g52)
    c: Coincident(g102,g52)
    c: Coincident(g102,g97)
    c: Weight(g103) = 1
    c: Equal(g103,g104)
    c: Equal(g103,g105)
    c: InternalAlignment(g103,g106)
    c: InternalAlignment(g104,g106)
    c: InternalAlignment(g105,g106)
    c: InternalAlignment(g107,g106)
    c: InternalAlignment(g108,g106)
    c: Weight(g109) = 1
    c: Equal(g109,g110)
    c: Equal(g109,g111)
    c: InternalAlignment(g109,g112)
    c: InternalAlignment(g110,g112)
    c: InternalAlignment(g111,g112)
    c: InternalAlignment(g113,g112)
    c: InternalAlignment(g114,g112)
    c: Block(g106)
    c: Block(g112)
    c: Coincident(g115,g106)
    c: Coincident(g115,g112)
    c: Vertical(g115)
    c: Coincident(g116,g112)
    c: Coincident(g116,g70)
    c: Coincident(g117,g70)
    c: Coincident(g117,g106)
    c: Weight(g118) = 1
    c: Equal(g118,g119)
    c: Equal(g118,g120)
    c: InternalAlignment(g118,g121)
    c: InternalAlignment(g119,g121)
    c: InternalAlignment(g120,g121)
    c: InternalAlignment(g122,g121)
    c: InternalAlignment(g123,g121)
    c: Weight(g124) = 1
    c: Equal(g124,g125)
    c: Equal(g124,g126)
    c: InternalAlignment(g124,g127)
    c: InternalAlignment(g125,g127)
    c: InternalAlignment(g126,g127)
    c: InternalAlignment(g128,g127)
    c: InternalAlignment(g129,g127)
    c: Block(g121)
    c: Block(g127)
    c: Coincident(g130,g121)
    c: Coincident(g130,g127)
    c: Vertical(g130)
    c: Coincident(g131,g127)
    c: Coincident(g131,g64)
    c: Coincident(g132,g64)
    c: Coincident(g132,g121)
    c: Weight(g133) = 1
    c: Equal(g133,g134)
    c: Equal(g133,g135)
    c: InternalAlignment(g133,g136)
    c: InternalAlignment(g134,g136)
    c: InternalAlignment(g135,g136)
    c: InternalAlignment(g137,g136)
    c: InternalAlignment(g138,g136)
    c: Weight(g139) = 1
    c: Equal(g139,g140)
    c: Equal(g139,g141)
    c: InternalAlignment(g139,g142)
    c: InternalAlignment(g140,g142)
    c: InternalAlignment(g141,g142)
    c: InternalAlignment(g143,g142)
    c: InternalAlignment(g144,g142)
    c: Weight(g145) = 1
    c: Equal(g145,g146)
    c: Equal(g145,g147)
    c: InternalAlignment(g145,g148)
    c: InternalAlignment(g146,g148)
    c: InternalAlignment(g147,g148)
    c: InternalAlignment(g149,g148)
    c: InternalAlignment(g150,g148)
    c: Weight(g151) = 1
    c: Equal(g151,g152)
    c: Equal(g151,g153)
    c: InternalAlignment(g151,g154)
    c: InternalAlignment(g152,g154)
    c: InternalAlignment(g153,g154)
    c: InternalAlignment(g155,g154)
    c: InternalAlignment(g156,g154)
    c: Block(g154)
    c: Block(g148)
    c: Block(g142)
    c: Block(g136)
    c: Coincident(g157,g31)
    c: Coincident(g157,g154)
    c: Coincident(g158,g154)
    c: Coincident(g158,g148)
    c: Horizontal(g158)
    c: Coincident(g159,g148)
    c: Coincident(g159,g31)
    c: Vertical(g159)
    c: Coincident(g160,g25)
    c: Coincident(g160,g142)
    c: Vertical(g160)
    c: Coincident(g161,g142)
    c: Coincident(g161,g136)
    c: Horizontal(g161)
    c: Coincident(g162,g136)
    c: Coincident(g162,g25)
    c: Weight(g163) = 1
    c: Equal(g163,g164)
    c: Equal(g163,g165)
    c: InternalAlignment(g163,g166)
    c: InternalAlignment(g164,g166)
    c: InternalAlignment(g165,g166)
    c: InternalAlignment(g167,g166)
    c: InternalAlignment(g168,g166)
    c: Weight(g169) = 1
    c: Equal(g169,g170)
    c: Equal(g169,g171)
    c: InternalAlignment(g169,g172)
    c: InternalAlignment(g170,g172)
    c: InternalAlignment(g171,g172)
    c: InternalAlignment(g173,g172)
    c: InternalAlignment(g174,g172)
    c: Weight(g175) = 1
    c: Equal(g175,g176)
    c: Equal(g175,g177)
    c: InternalAlignment(g175,g178)
    c: InternalAlignment(g176,g178)
    c: InternalAlignment(g177,g178)
    c: InternalAlignment(g179,g178)
    c: InternalAlignment(g180,g178)
    c: Weight(g181) = 1
    c: Equal(g181,g182)
    c: Equal(g181,g183)
    c: InternalAlignment(g181,g184)
    c: InternalAlignment(g182,g184)
    c: InternalAlignment(g183,g184)
    c: InternalAlignment(g185,g184)
    c: InternalAlignment(g186,g184)
    c: Block(g184)
    c: Block(g178)
    c: Block(g172)
    c: Block(g166)
    c: Coincident(g187,g184)
    c: Coincident(g187,g178)
    c: Horizontal(g187)
    c: Coincident(g188,g178)
    c: Coincident(g188,g13)
    c: Vertical(g188)
    c: Coincident(g189,g19)
    c: Coincident(g189,g172)
    c: Vertical(g189)
    c: Coincident(g190,g172)
    c: Coincident(g190,g166)
    c: Horizontal(g190)
    c: Coincident(g191,g166)
    c: Coincident(g191,g19)
    c: Coincident(g192,g13)
    c: Weight(g193) = 1
    c: Equal(g193,g194)
    c: Equal(g193,g195)
    c: InternalAlignment(g193,g196)
    c: InternalAlignment(g194,g196)
    c: InternalAlignment(g195,g196)
    c: InternalAlignment(g197,g196)
    c: InternalAlignment(g198,g196)
    c: Weight(g199) = 1
    c: Equal(g199,g200)
    c: Equal(g199,g201)
    c: InternalAlignment(g199,g202)
    c: InternalAlignment(g200,g202)
    c: InternalAlignment(g201,g202)
    c: InternalAlignment(g203,g202)
    c: InternalAlignment(g204,g202)
    c: Block(g202)
    c: Block(g196)
    c: Coincident(g205,g202)
    c: Coincident(g205,g37)
    c: Coincident(g206,g37)
    c: Coincident(g206,g196)
    c: Coincident(g207,g196)
    c: Coincident(g207,g202)
    c: Vertical(g207)
    c: Weight(g208) = 1
    c: Equal(g208,g209)
    c: Equal(g208,g210)
    c: InternalAlignment(g208,g211)
    c: InternalAlignment(g209,g211)
    c: InternalAlignment(g210,g211)
    c: InternalAlignment(g212,g211)
    c: InternalAlignment(g213,g211)
    c: Weight(g214) = 1
    c: Equal(g214,g215)
    c: Equal(g214,g216)
    c: InternalAlignment(g214,g217)
    c: InternalAlignment(g215,g217)
    c: InternalAlignment(g216,g217)
    c: InternalAlignment(g218,g217)
    c: InternalAlignment(g219,g217)
    c: Block(g217)
    c: Block(g211)
    c: Coincident(g220,g211)
    c: Coincident(g220,g43)
    c: Coincident(g221,g43)
    c: Coincident(g221,g217)
    c: Coincident(g222,g217)
    c: Coincident(g222,g211)
    c: Vertical(g222)
    c: Horizontal(g223)
    c: Block(g223)
    c: Vertical(g224)
    c: Block(g224)
    c: Block(g225)
    c: Weight(g226) = 1
    c: Equal(g226,g227)
    c: Equal(g226,g228)
    c: InternalAlignment(g226,g229)
    c: InternalAlignment(g227,g229)
    c: InternalAlignment(g228,g229)
    c: InternalAlignment(g230,g229)
    c: InternalAlignment(g231,g229)
    c: Weight(g232) = 1
    c: Equal(g232,g233)
    c: Equal(g232,g234)
    c: InternalAlignment(g232,g235)
    c: InternalAlignment(g233,g235)
    c: InternalAlignment(g234,g235)
    c: InternalAlignment(g236,g235)
    c: InternalAlignment(g237,g235)
    c: Weight(g238) = 1
    c: Equal(g238,g239)
    c: Equal(g238,g240)
    c: InternalAlignment(g238,g241)
    c: InternalAlignment(g239,g241)
    c: InternalAlignment(g240,g241)
    c: InternalAlignment(g242,g241)
    c: InternalAlignment(g243,g241)
    c: Weight(g244) = 1
    c: Equal(g244,g245)
    c: Equal(g244,g246)
    c: InternalAlignment(g244,g247)
    c: InternalAlignment(g245,g247)
    c: InternalAlignment(g246,g247)
    c: InternalAlignment(g248,g247)
    c: InternalAlignment(g249,g247)
    c: Block(g229)
    c: Block(g235)
    c: Block(g241)
    c: Block(g247)
    c: Coincident(g250,g235)
    c: Coincident(g250,g229)
    c: Horizontal(g250)
    c: Block(g192)
    c: Weight(g251) = 1
    c: Equal(g251,g252)
    c: Equal(g251,g253)
    c: InternalAlignment(g251,g254)
    c: InternalAlignment(g252,g254)
    c: InternalAlignment(g253,g254)
    c: InternalAlignment(g255,g254)
    c: InternalAlignment(g256,g254)
    c: Weight(g257) = 1
    c: Equal(g257,g258)
    c: Equal(g257,g259)
    c: InternalAlignment(g257,g260)
    c: InternalAlignment(g258,g260)
    c: InternalAlignment(g259,g260)
    c: InternalAlignment(g261,g260)
    c: InternalAlignment(g262,g260)
    c: Block(g254)
    c: Block(g260)
    c: Coincident(g263,g254)
    c: Coincident(g263,g260)
    c: Weight(g264) = 1
    c: Equal(g264,g265)
    c: Equal(g264,g266)
    c: InternalAlignment(g264,g267)
    c: InternalAlignment(g265,g267)
    c: InternalAlignment(g266,g267)
    c: InternalAlignment(g268,g267)
    c: InternalAlignment(g269,g267)
    c: Weight(g270) = 1
    c: Equal(g270,g271)
    c: Equal(g270,g272)
    c: InternalAlignment(g270,g273)
    c: InternalAlignment(g271,g273)
    c: InternalAlignment(g272,g273)
    c: InternalAlignment(g274,g273)
    c: InternalAlignment(g275,g273)
    c: Weight(g276) = 1
    c: Equal(g276,g277)
    c: Equal(g276,g278)
    c: InternalAlignment(g276,g279)
    c: InternalAlignment(g277,g279)
    c: InternalAlignment(g278,g279)
    c: InternalAlignment(g280,g279)
    c: InternalAlignment(g281,g279)
    c: Block(g279)
    c: Block(g273)
    c: Block(g267)
    c: Coincident(g282,g273)
    c: Coincident(g282,g267)
    c: Coincident(g283,g267)
    c: Coincident(g283,g279)
    c: Vertical(g283)
    c: Coincident(g284,g279)
    c: Coincident(g284,g273)
    c: Horizontal(g284)
    c: Weight(g285) = 1
    c: Equal(g285,g286)
    c: InternalAlignment(g285,g287)
    c: InternalAlignment(g286,g287)
    c: InternalAlignment(g288,g287)
    c: InternalAlignment(g289,g287)
    c: Weight(g290) = 1
    c: InternalAlignment(g291,g293)
    c: InternalAlignment(g292,g293)
    c: InternalAlignment(g294,g293)
    c: InternalAlignment(g295,g293)
    c: Weight(g296) = 1
    c: Equal(g296,g297)
    c: Equal(g296,g298)
    c: InternalAlignment(g296,g299)
    c: InternalAlignment(g297,g299)
    c: InternalAlignment(g298,g299)
    c: InternalAlignment(g300,g299)
    c: InternalAlignment(g301,g299)
    c: Equal(g302,g303)
    c: Equal(g302,g304)
    c: InternalAlignment(g302,g305)
    c: InternalAlignment(g303,g305)
    c: InternalAlignment(g304,g305)
    c: InternalAlignment(g306,g305)
    c: InternalAlignment(g307,g305)
    c: Block(g293)
    c: Block(g299)
    c: Block(g305)
    c: Block(g287)
    c: Coincident(g308,g287)
    c: Coincident(g308,g293)
    c: Horizontal(g308)
    c: Coincident(g309,g293)
    c: Coincident(g309,g299)
    c: Vertical(g309)
    c: Coincident(g310,g299)
    c: Coincident(g310,g305)
    c: Horizontal(g310)
    c: Coincident(g311,g305)
    c: Coincident(g311,g287)
    c: Weight(g312) = 1
    c: Equal(g312,g313)
    c: Equal(g312,g314)
    c: InternalAlignment(g312,g315)
    c: InternalAlignment(g313,g315)
    c: InternalAlignment(g314,g315)
    c: InternalAlignment(g316,g315)
    c: InternalAlignment(g317,g315)
    c: Weight(g318) = 1
    c: Equal(g318,g319)
    c: Equal(g318,g320)
    c: InternalAlignment(g318,g321)
    c: InternalAlignment(g319,g321)
    c: InternalAlignment(g320,g321)
    c: InternalAlignment(g322,g321)
    c: InternalAlignment(g323,g321)
    c: Weight(g324) = 1
    c: Equal(g324,g325)
    c: Equal(g324,g326)
    c: InternalAlignment(g324,g327)
    c: InternalAlignment(g325,g327)
    c: InternalAlignment(g326,g327)
    c: InternalAlignment(g328,g327)
    c: InternalAlignment(g329,g327)
    c: Block(g327)
    c: Block(g321)
    c: Block(g315)
    c: Coincident(g330,g327)
    c: Coincident(g330,g321)
    c: Horizontal(g330)
    c: Coincident(g331,g321)
    c: Coincident(g331,g315)
    c: Vertical(g331)
    c: Coincident(g332,g315)
    c: Coincident(g332,g327)
    c: InternalAlignment(g333,g334)
    c: InternalAlignment(g335,g334)
    c: InternalAlignment(g336,g334)
    c: Block(g334)
    c: Equal(g337,g338)
    c: Equal(g337,g339)
    c: InternalAlignment(g337,g340)
    c: InternalAlignment(g338,g340)
    c: InternalAlignment(g339,g340)
    c: InternalAlignment(g341,g340)
    c: InternalAlignment(g342,g340)
    c: Block(g340)
    c: Coincident(g343,g334)
    c: Horizontal(g343)
    c: Block(g343)
    c: Coincident(g344,g334)
    c: Coincident(g344,g260)
    c: Vertical(g344)
    c: Coincident(g345,g340)
    c: Coincident(g345,g254)
    c: Vertical(g345)
    c: Coincident(g347,g5)
    c: Coincident(g348,g5)
    c: Block(g346)
    c: Block(g5)
    c: Block(g348)
    c: Block(g347)
    c: Distance(g344) = 119.89
FEATURE [Sketcher::SketchObject] Sketch001
  FullyConstrained = true
  MapMode = 4
  Placement = pos=(0,0,0) rot=(0.57735,0.57735,0.57735;2.0944rad)
  Support = -> [Sketch]
  sketch-geometry (46):
    g0: BSplineCurve PolesCount=3 KnotsCount=2 Degree=2 IsPeriodic=0
    g1: ArcOfCircle CenterX=73.1223 CenterY=-32.291 CenterZ=0 NormalX=0 NormalY=0 NormalZ=1 AngleXU=0 Radius=13 StartAngle=5.92268 EndAngle=9.06428
    g2: ArcOfCircle CenterX=66.7816 CenterY=-49.1439 CenterZ=0 NormalX=0 NormalY=0 NormalZ=1 AngleXU=0 Radius=13 StartAngle=2.78068 EndAngle=5.92131
    g3: ArcOfCircle CenterX=55.9263 CenterY=-78.1807 CenterZ=0 NormalX=0 NormalY=0 NormalZ=1 AngleXU=0 Radius=13 StartAngle=5.92268 EndAngle=9.06428
    g4: ArcOfCircle CenterX=49.5884 CenterY=-95.0342 CenterZ=0 NormalX=0 NormalY=0 NormalZ=1 AngleXU=0 Radius=13 StartAngle=2.78068 EndAngle=5.92131
    g5: ArcOfCircle CenterX=38.7206 CenterY=-124.067 CenterZ=0 NormalX=0 NormalY=0 NormalZ=1 AngleXU=0 Radius=13 StartAngle=5.92268 EndAngle=9.06428
    g6: ArcOfCircle CenterX=32.3875 CenterY=-140.92 CenterZ=0 NormalX=0 NormalY=0 NormalZ=1 AngleXU=0 Radius=13 StartAngle=2.78068 EndAngle=5.92131
    g7: ArcOfCircle CenterX=21.4715 CenterY=-169.934 CenterZ=0 NormalX=0 NormalY=0 NormalZ=1 AngleXU=0 Radius=13 StartAngle=5.92268 EndAngle=9.06428
    g8: ArcOfCircle CenterX=15.1336 CenterY=-186.787 CenterZ=0 NormalX=0 NormalY=0 NormalZ=1 AngleXU=0 Radius=13 StartAngle=2.78068 EndAngle=5.92131
    g9-g12: Circle x4 (B-spline internal-alignment scaffolding for g13; pole/knot coordinates omitted)
    g13: BSplineCurve PolesCount=4 KnotsCount=2 Degree=3 IsPeriodic=0
    g14: GeomPoint X=28.8094 Y=-19.0875 Z=0
    g15: GeomPoint X=47.0443 Y=-50.4712 Z=0
    g16: Circle CenterX=53.5586 CenterY=-23.2695 CenterZ=0 NormalX=0 NormalY=0 NormalZ=1 AngleXU=0 Radius=3.24518
    g17: Circle CenterX=-195.441 CenterY=-127.082 CenterZ=0 NormalX=0 NormalY=0 NormalZ=1 AngleXU=0 Radius=1
    g18: Circle CenterX=-8.24091 CenterY=-197.481 CenterZ=0 NormalX=0 NormalY=0 NormalZ=1 AngleXU=0 Radius=1
    g19: Circle CenterX=12.8789 CenterY=-141.321 CenterZ=0 NormalX=0 NormalY=0 NormalZ=1 AngleXU=0 Radius=1
    g20: BSplineCurve PolesCount=3 KnotsCount=2 Degree=2 IsPeriodic=0
    g21: GeomPoint X=-195.441 Y=-127.082 Z=0
    g22: GeomPoint X=12.8789 Y=-141.321 Z=0
    g23: Circle CenterX=-12.8016 CenterY=-179.036 CenterZ=0 NormalX=0 NormalY=0 NormalZ=1 AngleXU=0 Radius=10.5072
    g24: Circle CenterX=0.933922 CenterY=-166.43 CenterZ=0 NormalX=0 NormalY=0 NormalZ=1 AngleXU=0 Radius=3.26661
    g25: Circle CenterX=-33.5518 CenterY=-176.44 CenterZ=0 NormalX=0 NormalY=0 NormalZ=1 AngleXU=0 Radius=5.64388
    g26: Circle CenterX=-47.2366 CenterY=-173.859 CenterZ=0 NormalX=0 NormalY=0 NormalZ=1 AngleXU=0 Radius=3.01653
    g27: Circle CenterX=-56.2595 CenterY=-171.456 CenterZ=0 NormalX=0 NormalY=0 NormalZ=1 AngleXU=0 Radius=2.12826
    g28: ArcOfCircle CenterX=51.2151 CenterY=-198.473 CenterZ=0 NormalX=0 NormalY=0 NormalZ=1 AngleXU=0 Radius=20 StartAngle=2.78189 EndAngle=4.35269
    g29: LineSegment StartX=32.4951 StartY=-191.433 StartZ=0 EndX=94.6578 EndY=-26.1352 EndZ=0
    g30: LineSegment StartX=43.1192 StartY=-220.001 StartZ=0 EndX=-196.497 EndY=-129.89 EndZ=0
    g31: LineSegment StartX=43.1192 StartY=-220.001 StartZ=0 EndX=44.1752 EndY=-217.193 EndZ=0
    g32: LineSegment StartX=117.223 StartY=-19.0875 StartZ=0 EndX=117.223 EndY=-16.0875 EndZ=0
    g33: LineSegment StartX=117.223 StartY=-16.0875 StartZ=0 EndX=17.2232 EndY=-16.0875 EndZ=0
    g34: LineSegment StartX=17.2232 StartY=-16.0875 StartZ=0 EndX=17.2232 EndY=-19.0875 EndZ=0
    g35: LineSegment StartX=28.8094 StartY=-19.0875 StartZ=0 EndX=17.2232 EndY=-19.0875 EndZ=0
    g36: LineSegment StartX=47.0443 StartY=-50.4712 StartZ=0 EndX=12.8789 EndY=-141.321 EndZ=0
    g37: LineSegment StartX=-195.441 StartY=-127.082 StartZ=0 EndX=-196.497 EndY=-129.89 EndZ=0
    g38: LineSegment StartX=85.2866 StartY=-36.8766 StartZ=0 EndX=78.9396 EndY=-53.7463 EndZ=0
    g39: LineSegment StartX=60.9579 StartY=-27.7053 StartZ=0 EndX=54.6191 EndY=-44.5532 EndZ=0
    g40: LineSegment StartX=68.0907 StartY=-82.7664 StartZ=0 EndX=61.7465 EndY=-99.6365 EndZ=0
    g41: LineSegment StartX=43.7619 StartY=-73.595 StartZ=0 EndX=37.426 EndY=-90.4435 EndZ=0
    g42: LineSegment StartX=50.885 StartY=-128.652 StartZ=0 EndX=44.5456 EndY=-145.522 EndZ=0
    g43: LineSegment StartX=26.5562 StartY=-119.481 StartZ=0 EndX=20.2251 EndY=-136.329 EndZ=0
    g44: LineSegment StartX=9.3071 StartY=-165.349 StartZ=0 EndX=2.97115 EndY=-182.197 EndZ=0
    g45: LineSegment StartX=33.6358 StartY=-174.52 StartZ=0 EndX=27.2917 EndY=-191.39 EndZ=0
  constraints (71):
    c: Block(g0)
    c: Block(g1)
    c: Block(g2)
    c: Block(g4)
    c: Block(g3)
    c: Block(g6)
    c: Block(g5)
    c: Block(g8)
    c: Block(g7)
    c: Weight(g9) = 1
    c: Equal(g9,g10)
    c: Equal(g9,g11)
    c: Equal(g9,g12)
    c: InternalAlignment(g9-g12 -> g13) x4
    c: InternalAlignment(g14,g13)
    c: InternalAlignment(g15,g13)
    c: Block(g16)
    c: Weight(g17) = 1
    c: Equal(g17,g18)
    c: Equal(g17,g19)
    c: InternalAlignment(g17,g20)
    c: InternalAlignment(g18,g20)
    c: InternalAlignment(g19,g20)
    c: InternalAlignment(g21,g20)
    c: InternalAlignment(g22,g20)
    c: Block(g20)
    c: Block(g23)
    c: Block(g24)
    c: Block(g25)
    c: Block(g26)
    c: Block(g27)
    c: Block(g28)
    c: Coincident(g29,g28)
    c: Coincident(g29,g0)
    c: Block(g13)
    c: Coincident(g31,g30)
    c: Coincident(g31,g28)
    c: Block(g31)
    c: Coincident(g32,g0)
    c: Vertical(g32)
    c: Coincident(g33,g32)
    c: Horizontal(g33)
    c: Coincident(g34,g33)
    c: Vertical(g34)
    c: Block(g33)
    c: Coincident(g35,g13)
    c: Coincident(g35,g34)
    c: Horizontal(g35)
    c: Coincident(g36,g13)
    c: Coincident(g36,g20)
    c: Coincident(g37,g20)
    c: Coincident(g37,g30)
    c: Block(g30)
    c: Coincident(g38,g1)
    c: Coincident(g38,g2)
    c: Coincident(g39,g1)
    c: Coincident(g39,g2)
    c: Coincident(g40,g3)
    c: Coincident(g40,g4)
    c: Coincident(g41,g3)
    c: Coincident(g41,g4)
    c: Coincident(g42,g5)
    c: Coincident(g42,g6)
    c: Coincident(g43,g5)
    c: Coincident(g43,g6)
    c: Coincident(g44,g7)
    c: Coincident(g44,g8)
    c: Coincident(g45,g7)
    c: Coincident(g45,g8)
    c: Distance(g30) = 256
    c: Distance(g33) = 100
FEATURE [Part::Extrusion] Extrude002
  Base = -> Sketch001
  Dir = (1,0,0)
  DirMode = 2
  FaceMakerClass = Part::FaceMakerBullseye
  LengthFwd = 8
  LengthRev = 0
  Solid = true
  Symmetric = false
FEATURE [Sketcher::SketchObject] Sketch002
  FullyConstrained = true
  sketch-geometry (20):
    g0: LineSegment StartX=-2.77179 StartY=-200.304 StartZ=0 EndX=5.22821 EndY=-200.304 EndZ=0
    g1: LineSegment StartX=5.22821 StartY=-200.304 StartZ=0 EndX=5.22821 EndY=-197.304 EndZ=0
    g2: LineSegment StartX=-2.77179 StartY=-200.304 StartZ=0 EndX=-2.77179 EndY=-197.304 EndZ=0
    g3: LineSegment StartX=5.22821 StartY=-197.304 StartZ=0 EndX=8.22821 EndY=-197.304 EndZ=0
    g4: LineSegment StartX=-2.77179 StartY=-197.304 StartZ=0 EndX=-5.77179 EndY=-197.304 EndZ=0
    g5: LineSegment StartX=19.2282 StartY=-203.304 StartZ=0 EndX=19.2282 EndY=-206.304 EndZ=0
    g6: LineSegment StartX=-16.7718 StartY=-203.304 StartZ=0 EndX=-16.7718 EndY=-206.304 EndZ=0
    g7: LineSegment StartX=-16.7718 StartY=-206.304 StartZ=0 EndX=19.2282 EndY=-206.304 EndZ=0
    g8: Circle CenterX=-16.7718 CenterY=-203.304 CenterZ=0 NormalX=0 NormalY=0 NormalZ=1 AngleXU=0 Radius=1
    g9: Circle CenterX=-5.77179 CenterY=-203.304 CenterZ=0 NormalX=0 NormalY=0 NormalZ=1 AngleXU=0 Radius=1
    g10: Circle CenterX=-5.77179 CenterY=-197.304 CenterZ=0 NormalX=0 NormalY=0 NormalZ=1 AngleXU=0 Radius=1
    g11: BSplineCurve PolesCount=3 KnotsCount=2 Degree=2 IsPeriodic=0
    g12: GeomPoint X=-16.7718 Y=-203.304 Z=0
    g13: GeomPoint X=-5.77179 Y=-197.304 Z=0
    g14: Circle CenterX=19.2282 CenterY=-203.304 CenterZ=0 NormalX=0 NormalY=0 NormalZ=1 AngleXU=0 Radius=1
    g15: Circle CenterX=8.22821 CenterY=-203.304 CenterZ=0 NormalX=0 NormalY=0 NormalZ=1 AngleXU=0 Radius=1
    g16: Circle CenterX=8.22821 CenterY=-197.304 CenterZ=0 NormalX=0 NormalY=0 NormalZ=1 AngleXU=0 Radius=1
    g17: BSplineCurve PolesCount=3 KnotsCount=2 Degree=2 IsPeriodic=0
    g18: GeomPoint X=19.2282 Y=-203.304 Z=0
    g19: GeomPoint X=8.22821 Y=-197.304 Z=0
  constraints (41):
    c: Horizontal(g0)
    c: Distance(g0) = 8
    c: Coincident(g1,g0)
    c: Vertical(g1)
    c: Distance(g1) = 3
    c: Coincident(g2,g0)
    c: Vertical(g2)
    c: Distance(g2) = 3
    c: Coincident(g3,g1)
    c: Horizontal(g3)
    c: Distance(g3) = 3
    c: Coincident(g4,g2)
    c: Horizontal(g4)
    c: Distance(g4) = 3
    c: Vertical(g5)
    c: Vertical(g6)
    c: Coincident(g7,g6)
    c: Coincident(g7,g5)
    c: Weight(g8) = 1
    c: Equal(g8,g9)
    c: Equal(g8,g10)
    c: Coincident(g11,g4)
    c: InternalAlignment(g8,g11)
    c: InternalAlignment(g9,g11)
    c: InternalAlignment(g10,g11)
    c: InternalAlignment(g12,g11)
    c: InternalAlignment(g13,g11)
    c: Coincident(g17,g5)
    c: Weight(g14) = 1
    c: Equal(g14,g15)
    c: Equal(g14,g16)
    c: Coincident(g17,g3)
    c: InternalAlignment(g14,g17)
    c: InternalAlignment(g15,g17)
    c: InternalAlignment(g16,g17)
    c: InternalAlignment(g18,g17)
    c: InternalAlignment(g19,g17)
    c: Block(g7)
    c: Block(g17)
    c: Block(g11)
    c: Block(g6)
FEATURE [Part::Extrusion] Extrude003
  Base = -> Sketch002
  Dir = (0,0,1)
  DirMode = 2
  FaceMakerClass = Part::FaceMakerBullseye
  LengthFwd = 260
  LengthRev = 0
  Solid = true
  Symmetric = false
FEATURE [Sketcher::SketchObject] Sketch003
  FullyConstrained = false
  sketch-geometry (410):
    g0: LineSegment StartX=-42.9272 StartY=136.221 StartZ=0 EndX=-42.9272 EndY=-103.779 EndZ=0
    g1: LineSegment StartX=407.073 StartY=136.221 StartZ=0 EndX=407.073 EndY=-103.779 EndZ=0
    g2: ArcOfCircle CenterX=-26.9272 CenterY=-83.7794 CenterZ=0 NormalX=0 NormalY=0 NormalZ=1 AngleXU=0 Radius=8 StartAngle=3.14159 EndAngle=6.28319
    g3: ArcOfCircle CenterX=391.073 CenterY=-83.7794 CenterZ=0 NormalX=0 NormalY=0 NormalZ=1 AngleXU=0 Radius=8 StartAngle=3.14159 EndAngle=6.28319
    g4: Circle CenterX=175.022 CenterY=27.0628 CenterZ=0 NormalX=0 NormalY=0 NormalZ=1 AngleXU=0 Radius=1
    g5: Circle CenterX=179.022 CenterY=24.8665 CenterZ=0 NormalX=0 NormalY=0 NormalZ=1 AngleXU=0 Radius=1
    g6: Circle CenterX=179.022 CenterY=27.0628 CenterZ=0 NormalX=0 NormalY=0 NormalZ=1 AngleXU=0 Radius=1
    g7: BSplineCurve PolesCount=3 KnotsCount=2 Degree=2 IsPeriodic=0
    g8: GeomPoint X=175.022 Y=27.0628 Z=0
    g9: GeomPoint X=179.022 Y=27.0628 Z=0
    g10: Circle CenterX=189.124 CenterY=27.0628 CenterZ=0 NormalX=0 NormalY=0 NormalZ=1 AngleXU=0 Radius=1
    g11: Circle CenterX=185.124 CenterY=24.8665 CenterZ=0 NormalX=0 NormalY=0 NormalZ=1 AngleXU=0 Radius=1
    g12: Circle CenterX=185.124 CenterY=27.0628 CenterZ=0 NormalX=0 NormalY=0 NormalZ=1 AngleXU=0 Radius=1
    g13: BSplineCurve PolesCount=3 KnotsCount=2 Degree=2 IsPeriodic=0
    g14: GeomPoint X=189.124 Y=27.0628 Z=0
    g15: GeomPoint X=185.124 Y=27.0628 Z=0
    g16: Circle CenterX=175.022 CenterY=5.37834 CenterZ=0 NormalX=0 NormalY=0 NormalZ=1 AngleXU=0 Radius=1
    g17: Circle CenterX=179.022 CenterY=7.57463 CenterZ=0 NormalX=0 NormalY=0 NormalZ=1 AngleXU=0 Radius=1
    g18: Circle CenterX=179.022 CenterY=5.34704 CenterZ=0 NormalX=0 NormalY=0 NormalZ=1 AngleXU=0 Radius=1
    g19: BSplineCurve PolesCount=3 KnotsCount=2 Degree=2 IsPeriodic=0
    g20: GeomPoint X=175.022 Y=5.37834 Z=0
    g21: GeomPoint X=179.022 Y=5.34704 Z=0
    g22: Circle CenterX=189.124 CenterY=5.37834 CenterZ=0 NormalX=0 NormalY=0 NormalZ=1 AngleXU=0 Radius=1
    g23: Circle CenterX=185.124 CenterY=7.57463 CenterZ=0 NormalX=0 NormalY=0 NormalZ=1 AngleXU=0 Radius=1
    g24: Circle CenterX=185.124 CenterY=5.34704 CenterZ=0 NormalX=0 NormalY=0 NormalZ=1 AngleXU=0 Radius=1
    g25: BSplineCurve PolesCount=3 KnotsCount=2 Degree=2 IsPeriodic=0
    g26: GeomPoint X=189.124 Y=5.37834 Z=0
    g27: GeomPoint X=185.124 Y=5.34704 Z=0
    g28: Circle CenterX=165.871 CenterY=18.1458 CenterZ=0 NormalX=0 NormalY=0 NormalZ=1 AngleXU=0 Radius=1
    g29: Circle CenterX=169.377 CenterY=16.2206 CenterZ=0 NormalX=0 NormalY=0 NormalZ=1 AngleXU=0 Radius=1
    g30: Circle CenterX=165.871 CenterY=14.2954 CenterZ=0 NormalX=0 NormalY=0 NormalZ=1 AngleXU=0 Radius=1
    g31: BSplineCurve PolesCount=3 KnotsCount=2 Degree=2 IsPeriodic=0
    g32: GeomPoint X=165.871 Y=18.1458 Z=0
    g33: GeomPoint X=165.871 Y=14.2954 Z=0
    g34: Circle CenterX=198.275 CenterY=18.1458 CenterZ=0 NormalX=0 NormalY=0 NormalZ=1 AngleXU=0 Radius=1
    g35: Circle CenterX=194.768 CenterY=16.2206 CenterZ=0 NormalX=0 NormalY=0 NormalZ=1 AngleXU=0 Radius=1
    g36: Circle CenterX=198.275 CenterY=14.2954 CenterZ=0 NormalX=0 NormalY=0 NormalZ=1 AngleXU=0 Radius=1
    g37: BSplineCurve PolesCount=3 KnotsCount=2 Degree=2 IsPeriodic=0
    g38: GeomPoint X=198.275 Y=18.1458 Z=0
    g39: GeomPoint X=198.275 Y=14.2954 Z=0
    g40: LineSegment StartX=407.073 StartY=-103.779 StartZ=0 EndX=-42.9272 EndY=-103.779 EndZ=0
    g41: Circle CenterX=125.607 CenterY=54.1951 CenterZ=0 NormalX=0 NormalY=0 NormalZ=1 AngleXU=0 Radius=1
    g42: Circle CenterX=139.632 CenterY=46.4944 CenterZ=0 NormalX=0 NormalY=0 NormalZ=1 AngleXU=0 Radius=1
    g43: Circle CenterX=127.326 CenterY=56.7187 CenterZ=0 NormalX=0 NormalY=0 NormalZ=1 AngleXU=0 Radius=1
    g44: BSplineCurve PolesCount=3 KnotsCount=2 Degree=2 IsPeriodic=0
    g45: GeomPoint X=125.607 Y=54.1951 Z=0
    g46: GeomPoint X=127.326 Y=56.7187 Z=0
    g47: Circle CenterX=236.821 CenterY=56.7187 CenterZ=0 NormalX=0 NormalY=0 NormalZ=1 AngleXU=0 Radius=1
    g48: Circle CenterX=224.513 CenterY=46.4944 CenterZ=0 NormalX=0 NormalY=0 NormalZ=1 AngleXU=0 Radius=1
    g49: Circle CenterX=238.538 CenterY=54.1951 CenterZ=0 NormalX=0 NormalY=0 NormalZ=1 AngleXU=0 Radius=1
    g50: BSplineCurve PolesCount=3 KnotsCount=2 Degree=2 IsPeriodic=0
    g51: GeomPoint X=236.821 Y=56.7187 Z=0
    g52: GeomPoint X=238.538 Y=54.1951 Z=0
    g53: Circle CenterX=238.538 CenterY=-21.7539 CenterZ=0 NormalX=0 NormalY=0 NormalZ=1 AngleXU=0 Radius=1
    g54: Circle CenterX=224.513 CenterY=-14.0532 CenterZ=0 NormalX=0 NormalY=0 NormalZ=1 AngleXU=0 Radius=1
    g55: Circle CenterX=236.821 CenterY=-24.2775 CenterZ=0 NormalX=0 NormalY=0 NormalZ=1 AngleXU=0 Radius=1
    g56: BSplineCurve PolesCount=3 KnotsCount=2 Degree=2 IsPeriodic=0
    g57: GeomPoint X=238.538 Y=-21.7539 Z=0
    g58: GeomPoint X=236.821 Y=-24.2775 Z=0
    g59: Circle CenterX=125.607 CenterY=-21.7539 CenterZ=0 NormalX=0 NormalY=0 NormalZ=1 AngleXU=0 Radius=1
    g60: Circle CenterX=139.632 CenterY=-14.0532 CenterZ=0 NormalX=0 NormalY=0 NormalZ=1 AngleXU=0 Radius=1
    g61: Circle CenterX=127.325 CenterY=-24.2775 CenterZ=0 NormalX=0 NormalY=0 NormalZ=1 AngleXU=0 Radius=1
    g62: BSplineCurve PolesCount=3 KnotsCount=2 Degree=2 IsPeriodic=0
    g63: GeomPoint X=125.607 Y=-21.7539 Z=0
    g64: GeomPoint X=127.325 Y=-24.2775 Z=0
    g65: Circle CenterX=302.996 CenterY=111.695 CenterZ=0 NormalX=0 NormalY=0 NormalZ=1 AngleXU=0 Radius=1
    g66: Circle CenterX=306.073 CenterY=114.251 CenterZ=0 NormalX=0 NormalY=0 NormalZ=1 AngleXU=0 Radius=1
    g67: Circle CenterX=306.073 CenterY=110.251 CenterZ=0 NormalX=0 NormalY=0 NormalZ=1 AngleXU=0 Radius=1
    g68: BSplineCurve PolesCount=3 KnotsCount=2 Degree=2 IsPeriodic=0
    g69: GeomPoint X=302.996 Y=111.695 Z=0
    g70: GeomPoint X=306.073 Y=110.251 Z=0
    g71: Circle CenterX=306.073 CenterY=95.2763 CenterZ=0 NormalX=0 NormalY=0 NormalZ=1 AngleXU=0 Radius=1
    g72: Circle CenterX=306.073 CenterY=91.2763 CenterZ=0 NormalX=0 NormalY=0 NormalZ=1 AngleXU=0 Radius=1
    g73: Circle CenterX=302.567 CenterY=89.3511 CenterZ=0 NormalX=0 NormalY=0 NormalZ=1 AngleXU=0 Radius=1
    g74: BSplineCurve PolesCount=3 KnotsCount=2 Degree=2 IsPeriodic=0
    g75: GeomPoint X=306.073 Y=95.2763 Z=0
    g76: GeomPoint X=302.567 Y=89.3511 Z=0
    g77: LineSegment StartX=306.073 StartY=110.251 StartZ=0 EndX=306.073 EndY=95.2763 EndZ=0
    g78: LineSegment StartX=302.996 StartY=111.695 StartZ=0 EndX=236.821 EndY=56.7187 EndZ=0
    g79: LineSegment StartX=238.538 StartY=54.1951 StartZ=0 EndX=302.567 EndY=89.3511 EndZ=0
    g80: Circle CenterX=61.1496 CenterY=111.695 CenterZ=0 NormalX=0 NormalY=0 NormalZ=1 AngleXU=0 Radius=1
    g81: Circle CenterX=58.0728 CenterY=114.251 CenterZ=0 NormalX=0 NormalY=0 NormalZ=1 AngleXU=0 Radius=1
    g82: Circle CenterX=58.0728 CenterY=110.251 CenterZ=0 NormalX=0 NormalY=0 NormalZ=1 AngleXU=0 Radius=1
    g83: BSplineCurve PolesCount=3 KnotsCount=2 Degree=2 IsPeriodic=0
    g84: GeomPoint X=61.1496 Y=111.695 Z=0
    g85: GeomPoint X=58.0728 Y=110.251 Z=0
    g86: Circle CenterX=61.5791 CenterY=89.3511 CenterZ=0 NormalX=0 NormalY=0 NormalZ=1 AngleXU=0 Radius=1
    g87: Circle CenterX=58.0728 CenterY=91.2763 CenterZ=0 NormalX=0 NormalY=0 NormalZ=1 AngleXU=0 Radius=1
    g88: Circle CenterX=58.0728 CenterY=95.2763 CenterZ=0 NormalX=0 NormalY=0 NormalZ=1 AngleXU=0 Radius=1
    g89: BSplineCurve PolesCount=3 KnotsCount=2 Degree=2 IsPeriodic=0
    g90: GeomPoint X=61.5791 Y=89.3511 Z=0
    g91: GeomPoint X=58.0728 Y=95.2763 Z=0
    g92: LineSegment StartX=58.0728 StartY=110.251 StartZ=0 EndX=58.0728 EndY=95.2763 EndZ=0
    g93: LineSegment StartX=61.1496 StartY=111.695 StartZ=0 EndX=127.326 EndY=56.7187 EndZ=0
    g94: LineSegment StartX=125.607 StartY=54.1951 StartZ=0 EndX=61.5791 EndY=89.3511 EndZ=0
    g95: Circle CenterX=61.5791 CenterY=-56.9099 CenterZ=0 NormalX=0 NormalY=0 NormalZ=1 AngleXU=0 Radius=1
    g96: Circle CenterX=58.0728 CenterY=-58.8351 CenterZ=0 NormalX=0 NormalY=0 NormalZ=1 AngleXU=0 Radius=1
    g97: Circle CenterX=58.0728 CenterY=-62.8351 CenterZ=0 NormalX=0 NormalY=0 NormalZ=1 AngleXU=0 Radius=1
    g98: BSplineCurve PolesCount=3 KnotsCount=2 Degree=2 IsPeriodic=0
    g99: GeomPoint X=61.5791 Y=-56.9099 Z=0
    g100: GeomPoint X=58.0728 Y=-62.8351 Z=0
    g101: Circle CenterX=58.0728 CenterY=-77.8102 CenterZ=0 NormalX=0 NormalY=0 NormalZ=1 AngleXU=0 Radius=1
    g102: Circle CenterX=58.0728 CenterY=-81.8102 CenterZ=0 NormalX=0 NormalY=0 NormalZ=1 AngleXU=0 Radius=1
    g103: Circle CenterX=61.1496 CenterY=-79.2541 CenterZ=0 NormalX=0 NormalY=0 NormalZ=1 AngleXU=0 Radius=1
    g104: BSplineCurve PolesCount=3 KnotsCount=2 Degree=2 IsPeriodic=0
    g105: GeomPoint X=58.0728 Y=-77.8102 Z=0
    g106: GeomPoint X=61.1496 Y=-79.2541 Z=0
    g107: LineSegment StartX=58.0728 StartY=-62.8351 StartZ=0 EndX=58.0728 EndY=-77.8102 EndZ=0
    g108: LineSegment StartX=61.1496 StartY=-79.2541 StartZ=0 EndX=127.325 EndY=-24.2775 EndZ=0
    g109: LineSegment StartX=125.607 StartY=-21.7539 StartZ=0 EndX=61.5791 EndY=-56.9099 EndZ=0
    g110: Circle CenterX=302.567 CenterY=-56.9099 CenterZ=0 NormalX=0 NormalY=0 NormalZ=1 AngleXU=0 Radius=1
    g111: Circle CenterX=306.073 CenterY=-58.8351 CenterZ=0 NormalX=0 NormalY=0 NormalZ=1 AngleXU=0 Radius=1
    g112: Circle CenterX=306.073 CenterY=-62.8351 CenterZ=0 NormalX=0 NormalY=0 NormalZ=1 AngleXU=0 Radius=1
    g113: BSplineCurve PolesCount=3 KnotsCount=2 Degree=2 IsPeriodic=0
    g114: GeomPoint X=302.567 Y=-56.9099 Z=0
    g115: GeomPoint X=306.073 Y=-62.8351 Z=0
    g116: Circle CenterX=302.996 CenterY=-79.2541 CenterZ=0 NormalX=0 NormalY=0 NormalZ=1 AngleXU=0 Radius=1
    g117: Circle CenterX=306.073 CenterY=-81.8102 CenterZ=0 NormalX=0 NormalY=0 NormalZ=1 AngleXU=0 Radius=1
    g118: Circle CenterX=306.073 CenterY=-77.8102 CenterZ=0 NormalX=0 NormalY=0 NormalZ=1 AngleXU=0 Radius=1
    g119: BSplineCurve PolesCount=3 KnotsCount=2 Degree=2 IsPeriodic=0
    g120: GeomPoint X=302.996 Y=-79.2541 Z=0
    g121: GeomPoint X=306.073 Y=-77.8102 Z=0
    g122: LineSegment StartX=306.073 StartY=-62.8351 StartZ=0 EndX=306.073 EndY=-77.8102 EndZ=0
    g123: LineSegment StartX=302.996 StartY=-79.2541 StartZ=0 EndX=236.821 EndY=-24.2775 EndZ=0
    g124: LineSegment StartX=238.538 StartY=-21.7539 StartZ=0 EndX=302.567 EndY=-56.9099 EndZ=0
    g125: Circle CenterX=61.6457 CenterY=-88.8112 CenterZ=0 NormalX=0 NormalY=0 NormalZ=1 AngleXU=0 Radius=1
    g126: Circle CenterX=58.0728 CenterY=-91.7794 CenterZ=0 NormalX=0 NormalY=0 NormalZ=1 AngleXU=0 Radius=1
    g127: Circle CenterX=63.9135 CenterY=-91.7794 CenterZ=0 NormalX=0 NormalY=0 NormalZ=1 AngleXU=0 Radius=1
    g128: BSplineCurve PolesCount=3 KnotsCount=2 Degree=2 IsPeriodic=0
    g129: GeomPoint X=61.6457 Y=-88.8112 Z=0
    g130: GeomPoint X=63.9135 Y=-91.7794 Z=0
    g131: Circle CenterX=179.022 CenterY=-85.8163 CenterZ=0 NormalX=0 NormalY=0 NormalZ=1 AngleXU=0 Radius=1
    g132: Circle CenterX=179.022 CenterY=-91.7794 CenterZ=0 NormalX=0 NormalY=0 NormalZ=1 AngleXU=0 Radius=1
    g133: Circle CenterX=171.895 CenterY=-91.7794 CenterZ=0 NormalX=0 NormalY=0 NormalZ=1 AngleXU=0 Radius=1
    g134: BSplineCurve PolesCount=3 KnotsCount=2 Degree=2 IsPeriodic=0
    g135: GeomPoint X=179.022 Y=-85.8163 Z=0
    g136: GeomPoint X=171.895 Y=-91.7794 Z=0
    g137: Circle CenterX=185.124 CenterY=-86.2028 CenterZ=0 NormalX=0 NormalY=0 NormalZ=1 AngleXU=0 Radius=1
    g138: Circle CenterX=185.124 CenterY=-91.7794 CenterZ=0 NormalX=0 NormalY=0 NormalZ=1 AngleXU=0 Radius=1
    g139: Circle CenterX=191.747 CenterY=-91.7794 CenterZ=0 NormalX=0 NormalY=0 NormalZ=1 AngleXU=0 Radius=1
    g140: BSplineCurve PolesCount=3 KnotsCount=2 Degree=2 IsPeriodic=0
    g141: GeomPoint X=185.124 Y=-86.2028 Z=0
    g142: GeomPoint X=191.747 Y=-91.7794 Z=0
    g143: Circle CenterX=299.888 CenterY=-86.6413 CenterZ=0 NormalX=0 NormalY=0 NormalZ=1 AngleXU=0 Radius=1
    g144: Circle CenterX=306.073 CenterY=-91.7794 CenterZ=0 NormalX=0 NormalY=0 NormalZ=1 AngleXU=0 Radius=1
    g145: Circle CenterX=298.776 CenterY=-91.7794 CenterZ=0 NormalX=0 NormalY=0 NormalZ=1 AngleXU=0 Radius=1
    g146: BSplineCurve PolesCount=3 KnotsCount=2 Degree=2 IsPeriodic=0
    g147: GeomPoint X=299.888 Y=-86.6413 Z=0
    g148: GeomPoint X=298.776 Y=-91.7794 Z=0
    g149: LineSegment StartX=189.124 StartY=5.37834 StartZ=0 EndX=299.888 EndY=-86.6413 EndZ=0
    g150: LineSegment StartX=298.776 StartY=-91.7794 StartZ=0 EndX=191.747 EndY=-91.7794 EndZ=0
    g151: LineSegment StartX=185.124 StartY=-86.2028 StartZ=0 EndX=185.124 EndY=5.34704 EndZ=0
    g152: LineSegment StartX=179.022 StartY=5.34704 StartZ=0 EndX=179.022 EndY=-85.8163 EndZ=0
    g153: LineSegment StartX=171.895 StartY=-91.7794 StartZ=0 EndX=63.9135 EndY=-91.7794 EndZ=0
    g154: LineSegment StartX=61.6457 StartY=-88.8112 StartZ=0 EndX=175.022 EndY=5.37834 EndZ=0
    g155: Circle CenterX=302.073 CenterY=124.221 CenterZ=0 NormalX=0 NormalY=0 NormalZ=1 AngleXU=0 Radius=1
    g156: Circle CenterX=306.073 CenterY=124.221 CenterZ=0 NormalX=0 NormalY=0 NormalZ=1 AngleXU=0 Radius=1
    g157: Circle CenterX=302.996 CenterY=121.665 CenterZ=0 NormalX=0 NormalY=0 NormalZ=1 AngleXU=0 Radius=1
    g158: BSplineCurve PolesCount=3 KnotsCount=2 Degree=2 IsPeriodic=0
    g159: GeomPoint X=302.073 Y=124.221 Z=0
    g160: GeomPoint X=302.996 Y=121.665 Z=0
    g161: Circle CenterX=189.124 CenterY=124.221 CenterZ=0 NormalX=0 NormalY=0 NormalZ=1 AngleXU=0 Radius=1
    g162: Circle CenterX=185.124 CenterY=124.221 CenterZ=0 NormalX=0 NormalY=0 NormalZ=1 AngleXU=0 Radius=1
    g163: Circle CenterX=185.124 CenterY=120.221 CenterZ=0 NormalX=0 NormalY=0 NormalZ=1 AngleXU=0 Radius=1
    g164: BSplineCurve PolesCount=3 KnotsCount=2 Degree=2 IsPeriodic=0
    g165: GeomPoint X=189.124 Y=124.221 Z=0
    g166: GeomPoint X=185.124 Y=120.221 Z=0
    g167: Circle CenterX=175.022 CenterY=124.221 CenterZ=0 NormalX=0 NormalY=0 NormalZ=1 AngleXU=0 Radius=1
    g168: Circle CenterX=179.022 CenterY=124.221 CenterZ=0 NormalX=0 NormalY=0 NormalZ=1 AngleXU=0 Radius=1
    g169: Circle CenterX=179.022 CenterY=120.221 CenterZ=0 NormalX=0 NormalY=0 NormalZ=1 AngleXU=0 Radius=1
    g170: BSplineCurve PolesCount=3 KnotsCount=2 Degree=2 IsPeriodic=0
    g171: GeomPoint X=175.022 Y=124.221 Z=0
    g172: GeomPoint X=179.022 Y=120.221 Z=0
    g173: Circle CenterX=62.0728 CenterY=124.221 CenterZ=0 NormalX=0 NormalY=0 NormalZ=1 AngleXU=0 Radius=1
    g174: Circle CenterX=58.0728 CenterY=124.221 CenterZ=0 NormalX=0 NormalY=0 NormalZ=1 AngleXU=0 Radius=1
    g175: Circle CenterX=61.1496 CenterY=121.665 CenterZ=0 NormalX=0 NormalY=0 NormalZ=1 AngleXU=0 Radius=1
    g176: BSplineCurve PolesCount=3 KnotsCount=2 Degree=2 IsPeriodic=0
    g177: GeomPoint X=62.0728 Y=124.221 Z=0
    g178: GeomPoint X=61.1496 Y=121.665 Z=0
    g179: LineSegment StartX=179.022 StartY=120.221 StartZ=0 EndX=179.022 EndY=27.0628 EndZ=0
    g180: LineSegment StartX=185.124 StartY=27.0628 StartZ=0 EndX=185.124 EndY=120.221 EndZ=0
    g181: LineSegment StartX=302.996 StartY=121.665 StartZ=0 EndX=189.124 EndY=27.0628 EndZ=0
    g182: LineSegment StartX=175.022 StartY=27.0628 StartZ=0 EndX=61.1496 EndY=121.665 EndZ=0
    g183: Circle CenterX=61.5791 CenterY=75.4095 CenterZ=0 NormalX=0 NormalY=0 NormalZ=1 AngleXU=0 Radius=1
    g184: Circle CenterX=58.0728 CenterY=77.3346 CenterZ=0 NormalX=0 NormalY=0 NormalZ=1 AngleXU=0 Radius=1
    g185: Circle CenterX=58.0728 CenterY=73.3346 CenterZ=0 NormalX=0 NormalY=0 NormalZ=1 AngleXU=0 Radius=1
    g186: BSplineCurve PolesCount=3 KnotsCount=2 Degree=2 IsPeriodic=0
    g187: GeomPoint X=61.5791 Y=75.4095 Z=0
    g188: GeomPoint X=58.0728 Y=73.3346 Z=0
    g189: Circle CenterX=58.0728 CenterY=-40.8935 CenterZ=0 NormalX=0 NormalY=0 NormalZ=1 AngleXU=0 Radius=1
    g190: Circle CenterX=58.0728 CenterY=-44.8935 CenterZ=0 NormalX=0 NormalY=0 NormalZ=1 AngleXU=0 Radius=1
    g191: Circle CenterX=61.5791 CenterY=-42.9683 CenterZ=0 NormalX=0 NormalY=0 NormalZ=1 AngleXU=0 Radius=1
    g192: BSplineCurve PolesCount=3 KnotsCount=2 Degree=2 IsPeriodic=0
    g193: GeomPoint X=58.0728 Y=-40.8935 Z=0
    g194: GeomPoint X=61.5791 Y=-42.9683 Z=0
    g195: LineSegment StartX=61.5791 StartY=-42.9683 StartZ=0 EndX=165.871 EndY=14.2954 EndZ=0
    g196: LineSegment StartX=165.871 StartY=18.1458 StartZ=0 EndX=61.5791 EndY=75.4095 EndZ=0
    g197: LineSegment StartX=58.0728 StartY=73.3346 StartZ=0 EndX=58.0728 EndY=-40.8935 EndZ=0
    g198: Circle CenterX=302.567 CenterY=-42.9683 CenterZ=0 NormalX=0 NormalY=0 NormalZ=1 AngleXU=0 Radius=1
    g199: Circle CenterX=306.073 CenterY=-44.8935 CenterZ=0 NormalX=0 NormalY=0 NormalZ=1 AngleXU=0 Radius=1
    g200: Circle CenterX=306.073 CenterY=-40.8935 CenterZ=0 NormalX=0 NormalY=0 NormalZ=1 AngleXU=0 Radius=1
    g201: BSplineCurve PolesCount=3 KnotsCount=2 Degree=2 IsPeriodic=0
    g202: GeomPoint X=302.567 Y=-42.9683 Z=0
    g203: GeomPoint X=306.073 Y=-40.8935 Z=0
    g204: Circle CenterX=306.073 CenterY=73.3346 CenterZ=0 NormalX=0 NormalY=0 NormalZ=1 AngleXU=0 Radius=1
    g205: Circle CenterX=306.073 CenterY=77.3346 CenterZ=0 NormalX=0 NormalY=0 NormalZ=1 AngleXU=0 Radius=1
    g206: Circle CenterX=302.567 CenterY=75.4095 CenterZ=0 NormalX=0 NormalY=0 NormalZ=1 AngleXU=0 Radius=1
    g207: BSplineCurve PolesCount=3 KnotsCount=2 Degree=2 IsPeriodic=0
    g208: GeomPoint X=306.073 Y=73.3346 Z=0
    g209: GeomPoint X=302.567 Y=75.4095 Z=0
    g210: LineSegment StartX=302.567 StartY=-42.9683 StartZ=0 EndX=198.275 EndY=14.2954 EndZ=0
    g211: LineSegment StartX=198.275 StartY=18.1458 StartZ=0 EndX=302.567 EndY=75.4095 EndZ=0
    g212: LineSegment StartX=306.073 StartY=73.3346 StartZ=0 EndX=306.073 EndY=-40.8935 EndZ=0
    g213: LineSegment StartX=322.073 StartY=105.865 StartZ=0 EndX=328.643 EndY=105.865 EndZ=0
    g214: LineSegment StartX=318.073 StartY=120.221 StartZ=0 EndX=318.073 EndY=109.865 EndZ=0
    g215: LineSegment StartX=336.157 StartY=107.779 StartZ=0 EndX=362.567 EndY=122.294 EndZ=0
    g216: Circle CenterX=362.073 CenterY=124.221 CenterZ=0 NormalX=0 NormalY=0 NormalZ=1 AngleXU=0 Radius=1
    g217: Circle CenterX=366.073 CenterY=124.221 CenterZ=0 NormalX=0 NormalY=0 NormalZ=1 AngleXU=0 Radius=1
    g218: Circle CenterX=362.567 CenterY=122.294 CenterZ=0 NormalX=0 NormalY=0 NormalZ=1 AngleXU=0 Radius=1
    g219: BSplineCurve PolesCount=3 KnotsCount=2 Degree=2 IsPeriodic=0
    g220: GeomPoint X=362.073 Y=124.221 Z=0
    g221: GeomPoint X=362.567 Y=122.294 Z=0
    g222: Circle CenterX=322.073 CenterY=124.221 CenterZ=0 NormalX=0 NormalY=0 NormalZ=1 AngleXU=0 Radius=1
    g223: Circle CenterX=318.073 CenterY=124.221 CenterZ=0 NormalX=0 NormalY=0 NormalZ=1 AngleXU=0 Radius=1
    g224: Circle CenterX=318.073 CenterY=120.221 CenterZ=0 NormalX=0 NormalY=0 NormalZ=1 AngleXU=0 Radius=1
    g225: BSplineCurve PolesCount=3 KnotsCount=2 Degree=2 IsPeriodic=0
    g226: GeomPoint X=322.073 Y=124.221 Z=0
    g227: GeomPoint X=318.073 Y=120.221 Z=0
    g228: Circle CenterX=322.073 CenterY=105.865 CenterZ=0 NormalX=0 NormalY=0 NormalZ=1 AngleXU=0 Radius=1
    g229: Circle CenterX=318.073 CenterY=105.865 CenterZ=0 NormalX=0 NormalY=0 NormalZ=1 AngleXU=0 Radius=1
    g230: Circle CenterX=318.073 CenterY=109.865 CenterZ=0 NormalX=0 NormalY=0 NormalZ=1 AngleXU=0 Radius=1
    g231: BSplineCurve PolesCount=3 KnotsCount=2 Degree=2 IsPeriodic=0
    g232: GeomPoint X=322.073 Y=105.865 Z=0
    g233: GeomPoint X=318.073 Y=109.865 Z=0
    g234: Circle CenterX=336.157 CenterY=107.779 CenterZ=0 NormalX=0 NormalY=0 NormalZ=1 AngleXU=0 Radius=1
    g235: Circle CenterX=332.651 CenterY=105.853 CenterZ=0 NormalX=0 NormalY=0 NormalZ=1 AngleXU=0 Radius=1
    g236: Circle CenterX=328.643 CenterY=105.865 CenterZ=0 NormalX=0 NormalY=0 NormalZ=1 AngleXU=0 Radius=1
    g237: BSplineCurve PolesCount=3 KnotsCount=2 Degree=2 IsPeriodic=0
    g238: GeomPoint X=336.157 Y=107.779 Z=0
    g239: GeomPoint X=328.643 Y=105.865 Z=0
    g240: LineSegment StartX=322.073 StartY=124.221 StartZ=0 EndX=362.073 EndY=124.221 EndZ=0
    g241: Circle CenterX=371.567 CenterY=-80.8644 CenterZ=0 NormalX=0 NormalY=0 NormalZ=1 AngleXU=0 Radius=1
    g242: Circle CenterX=375.073 CenterY=-82.7896 CenterZ=0 NormalX=0 NormalY=0 NormalZ=1 AngleXU=0 Radius=1
    g243: Circle CenterX=375.073 CenterY=-78.7896 CenterZ=0 NormalX=0 NormalY=0 NormalZ=1 AngleXU=0 Radius=1
    g244: BSplineCurve PolesCount=3 KnotsCount=2 Degree=2 IsPeriodic=0
    g245: GeomPoint X=371.567 Y=-80.8644 Z=0
    g246: GeomPoint X=375.073 Y=-78.7896 Z=0
    g247: Circle CenterX=321.579 CenterY=-53.4075 CenterZ=0 NormalX=0 NormalY=0 NormalZ=1 AngleXU=0 Radius=1
    g248: Circle CenterX=318.073 CenterY=-51.4823 CenterZ=0 NormalX=0 NormalY=0 NormalZ=1 AngleXU=0 Radius=1
    g249: Circle CenterX=318.073 CenterY=-47.4805 CenterZ=0 NormalX=0 NormalY=0 NormalZ=1 AngleXU=0 Radius=1
    g250: BSplineCurve PolesCount=3 KnotsCount=2 Degree=2 IsPeriodic=0
    g251: GeomPoint X=321.579 Y=-53.4075 Z=0
    g252: GeomPoint X=318.073 Y=-47.4805 Z=0
    g253: LineSegment StartX=371.567 StartY=-80.8644 StartZ=0 EndX=321.579 EndY=-53.4075 EndZ=0
    g254: Circle CenterX=321.579 CenterY=-67.3492 CenterZ=0 NormalX=0 NormalY=0 NormalZ=1 AngleXU=0 Radius=1
    g255: Circle CenterX=318.073 CenterY=-65.424 CenterZ=0 NormalX=0 NormalY=0 NormalZ=1 AngleXU=0 Radius=1
    g256: Circle CenterX=318.073 CenterY=-69.424 CenterZ=0 NormalX=0 NormalY=0 NormalZ=1 AngleXU=0 Radius=1
    g257: BSplineCurve PolesCount=3 KnotsCount=2 Degree=2 IsPeriodic=0
    g258: GeomPoint X=321.579 Y=-67.3492 Z=0
    g259: GeomPoint X=318.073 Y=-69.424 Z=0
    g260: Circle CenterX=362.567 CenterY=-89.8542 CenterZ=0 NormalX=0 NormalY=0 NormalZ=1 AngleXU=0 Radius=1
    g261: Circle CenterX=366.073 CenterY=-91.7794 CenterZ=0 NormalX=0 NormalY=0 NormalZ=1 AngleXU=0 Radius=1
    g262: Circle CenterX=362.073 CenterY=-91.7794 CenterZ=0 NormalX=0 NormalY=0 NormalZ=1 AngleXU=0 Radius=1
    g263: BSplineCurve PolesCount=3 KnotsCount=2 Degree=2 IsPeriodic=0
    g264: GeomPoint X=362.567 Y=-89.8542 Z=0
    g265: GeomPoint X=362.073 Y=-91.7794 Z=0
    g266: Circle CenterX=322.073 CenterY=-91.7794 CenterZ=0 NormalX=0 NormalY=0 NormalZ=1 AngleXU=0 Radius=1
    g267: Circle CenterX=318.073 CenterY=-91.7794 CenterZ=0 NormalX=0 NormalY=0 NormalZ=1 AngleXU=0 Radius=1
    g268: Circle CenterX=318.073 CenterY=-87.7794 CenterZ=0 NormalX=0 NormalY=0 NormalZ=1 AngleXU=0 Radius=1
    g269: BSplineCurve PolesCount=3 KnotsCount=2 Degree=2 IsPeriodic=0
    g270: GeomPoint X=322.073 Y=-91.7794 Z=0
    g271: GeomPoint X=318.073 Y=-87.7794 Z=0
    g272: LineSegment StartX=362.567 StartY=-89.8542 StartZ=0 EndX=321.579 EndY=-67.3492 EndZ=0
    g273: LineSegment StartX=318.073 StartY=-69.424 StartZ=0 EndX=318.073 EndY=-87.7794 EndZ=0
    g274: LineSegment StartX=322.073 StartY=-91.7794 StartZ=0 EndX=362.073 EndY=-91.7794 EndZ=0
    g275: Circle CenterX=2.07281 CenterY=124.221 CenterZ=0 NormalX=0 NormalY=0 NormalZ=1 AngleXU=0 Radius=1
    g276: Circle CenterX=1.57905 CenterY=122.295 CenterZ=0 NormalX=0 NormalY=0 NormalZ=1 AngleXU=0 Radius=1
    g277: BSplineCurve PolesCount=3 KnotsCount=2 Degree=2 IsPeriodic=0
    g278: GeomPoint X=2.07281 Y=124.221 Z=0
    g279: GeomPoint X=1.57905 Y=122.295 Z=0
    g280: Circle CenterX=42.0728 CenterY=124.221 CenterZ=0 NormalX=0 NormalY=0 NormalZ=1 AngleXU=0 Radius=1
    g281: Circle CenterX=46.0728 CenterY=124.221 CenterZ=0 NormalX=0 NormalY=0 NormalZ=1 AngleXU=0 Radius=1
    g282: Circle CenterX=46.0728 CenterY=120.221 CenterZ=0 NormalX=0 NormalY=0 NormalZ=1 AngleXU=0 Radius=1
    g283: BSplineCurve PolesCount=3 KnotsCount=2 Degree=2 IsPeriodic=0
    g284: GeomPoint X=42.0728 Y=124.221 Z=0
    g285: GeomPoint X=46.0728 Y=120.221 Z=0
    g286: Circle CenterX=46.0728 CenterY=109.865 CenterZ=0 NormalX=0 NormalY=0 NormalZ=1 AngleXU=0 Radius=1
    g287: Circle CenterX=46.0728 CenterY=105.865 CenterZ=0 NormalX=0 NormalY=0 NormalZ=1 AngleXU=0 Radius=1
    g288: Circle CenterX=42.0728 CenterY=105.865 CenterZ=0 NormalX=0 NormalY=0 NormalZ=1 AngleXU=0 Radius=1
    g289: BSplineCurve PolesCount=3 KnotsCount=2 Degree=2 IsPeriodic=0
    g290: GeomPoint X=46.0728 Y=109.865 Z=0
    g291: GeomPoint X=42.0728 Y=105.865 Z=0
    g292: Circle CenterX=35.5028 CenterY=105.865 CenterZ=0 NormalX=0 NormalY=0 NormalZ=1 AngleXU=0 Radius=1
    g293: Circle CenterX=31.5028 CenterY=105.865 CenterZ=0 NormalX=0 NormalY=0 NormalZ=1 AngleXU=0 Radius=1
    g294: Circle CenterX=27.9965 CenterY=107.79 CenterZ=0 NormalX=0 NormalY=0 NormalZ=1 AngleXU=0 Radius=1
    g295: BSplineCurve PolesCount=3 KnotsCount=2 Degree=2 IsPeriodic=0
    g296: GeomPoint X=35.5028 Y=105.865 Z=0
    g297: GeomPoint X=27.9965 Y=107.79 Z=0
    g298: LineSegment StartX=2.07281 StartY=124.221 StartZ=0 EndX=42.0728 EndY=124.221 EndZ=0
    g299: LineSegment StartX=46.0728 StartY=120.221 StartZ=0 EndX=46.0728 EndY=109.865 EndZ=0
    g300: LineSegment StartX=42.0728 StartY=105.865 StartZ=0 EndX=35.5028 EndY=105.865 EndZ=0
    g301: LineSegment StartX=27.9965 StartY=107.79 StartZ=0 EndX=1.57905 EndY=122.295 EndZ=0
    g302: Circle CenterX=42.5666 CenterY=-67.3492 CenterZ=0 NormalX=0 NormalY=0 NormalZ=1 AngleXU=0 Radius=1
    g303: Circle CenterX=46.0728 CenterY=-65.424 CenterZ=0 NormalX=0 NormalY=0 NormalZ=1 AngleXU=0 Radius=1
    g304: Circle CenterX=46.0728 CenterY=-69.424 CenterZ=0 NormalX=0 NormalY=0 NormalZ=1 AngleXU=0 Radius=1
    g305: BSplineCurve PolesCount=3 KnotsCount=2 Degree=2 IsPeriodic=0
    g306: GeomPoint X=42.5666 Y=-67.3492 Z=0
    g307: GeomPoint X=46.0728 Y=-69.424 Z=0
    g308: Circle CenterX=46.0728 CenterY=-87.7794 CenterZ=0 NormalX=0 NormalY=0 NormalZ=1 AngleXU=0 Radius=1
    g309: Circle CenterX=46.0728 CenterY=-91.7794 CenterZ=0 NormalX=0 NormalY=0 NormalZ=1 AngleXU=0 Radius=1
    g310: Circle CenterX=42.0728 CenterY=-91.7794 CenterZ=0 NormalX=0 NormalY=0 NormalZ=1 AngleXU=0 Radius=1
    g311: BSplineCurve PolesCount=3 KnotsCount=2 Degree=2 IsPeriodic=0
    g312: GeomPoint X=46.0728 Y=-87.7794 Z=0
    g313: GeomPoint X=42.0728 Y=-91.7794 Z=0
    g314: Circle CenterX=2.07281 CenterY=-91.7794 CenterZ=0 NormalX=0 NormalY=0 NormalZ=1 AngleXU=0 Radius=1
    g315: Circle CenterX=-1.92719 CenterY=-91.7794 CenterZ=0 NormalX=0 NormalY=0 NormalZ=1 AngleXU=0 Radius=1
    g316: Circle CenterX=1.57905 CenterY=-89.8542 CenterZ=0 NormalX=0 NormalY=0 NormalZ=1 AngleXU=0 Radius=1
    g317: BSplineCurve PolesCount=3 KnotsCount=2 Degree=2 IsPeriodic=0
    g318: GeomPoint X=2.07281 Y=-91.7794 Z=0
    g319: GeomPoint X=1.57905 Y=-89.8542 Z=0
    g320: LineSegment StartX=2.07281 StartY=-91.7794 StartZ=0 EndX=42.0728 EndY=-91.7794 EndZ=0
    g321: LineSegment StartX=46.0728 StartY=-87.7794 StartZ=0 EndX=46.0728 EndY=-69.424 EndZ=0
    g322: LineSegment StartX=42.5666 StartY=-67.3492 StartZ=0 EndX=1.57905 EndY=-89.8542 EndZ=0
    g323: Circle CenterX=322.073 CenterY=76.4095 CenterZ=0 NormalX=0 NormalY=0 NormalZ=1 AngleXU=0 Radius=4
    g324: BSplineCurve PolesCount=3 KnotsCount=2 Degree=2 IsPeriodic=0
    g325: GeomPoint X=318.073 Y=72.4095 Z=0
    g326: GeomPoint X=322.073 Y=76.4095 Z=0
    g327: Circle CenterX=375.073 CenterY=72.4095 CenterZ=0 NormalX=0 NormalY=0 NormalZ=1 AngleXU=0 Radius=1
    g328: Circle CenterX=375.073 CenterY=76.4095 CenterZ=0 NormalX=0 NormalY=0 NormalZ=1 AngleXU=0 Radius=1
    g329: Circle CenterX=371.073 CenterY=76.4095 CenterZ=0 NormalX=0 NormalY=0 NormalZ=1 AngleXU=0 Radius=1
    g330: BSplineCurve PolesCount=3 KnotsCount=2 Degree=2 IsPeriodic=0
    g331: GeomPoint X=375.073 Y=72.4095 Z=0
    g332: GeomPoint X=371.073 Y=76.4095 Z=0
    g333: LineSegment StartX=322.073 StartY=76.4095 StartZ=0 EndX=371.073 EndY=76.4095 EndZ=0
    g334: LineSegment StartX=318.073 StartY=72.4095 StartZ=0 EndX=318.073 EndY=-47.4805 EndZ=0
    g335: LineSegment StartX=375.073 StartY=72.4095 StartZ=0 EndX=375.073 EndY=-78.7896 EndZ=0
    g336: ArcOfCircle CenterX=-26.9272 CenterY=22.1087 CenterZ=0 NormalX=0 NormalY=0 NormalZ=1 AngleXU=0 Radius=4 StartAngle=5e-16 EndAngle=3.14159
    g337: LineSegment StartX=-22.9272 StartY=22.1087 StartZ=0 EndX=-18.9272 EndY=-83.7794 EndZ=0
    g338: LineSegment StartX=-34.9272 StartY=-83.7794 StartZ=0 EndX=-30.9272 EndY=22.1087 EndZ=0
    g339: ArcOfCircle CenterX=391.073 CenterY=22.1087 CenterZ=0 NormalX=0 NormalY=0 NormalZ=1 AngleXU=0 Radius=4 StartAngle=0 EndAngle=3.14159
    g340: LineSegment StartX=387.073 StartY=22.1087 StartZ=0 EndX=383.073 EndY=-83.7794 EndZ=0
    g341: LineSegment StartX=395.073 StartY=22.1087 StartZ=0 EndX=399.073 EndY=-83.7794 EndZ=0
    g342: Circle CenterX=-10.9272 CenterY=-78.7794 CenterZ=0 NormalX=0 NormalY=0 NormalZ=1 AngleXU=0 Radius=1
    g343: Circle CenterX=-10.9272 CenterY=-82.7794 CenterZ=0 NormalX=0 NormalY=0 NormalZ=1 AngleXU=0 Radius=1
    g344: Circle CenterX=-7.42095 CenterY=-80.8542 CenterZ=0 NormalX=0 NormalY=0 NormalZ=1 AngleXU=0 Radius=1
    g345: BSplineCurve PolesCount=3 KnotsCount=2 Degree=2 IsPeriodic=0
    g346: GeomPoint X=-10.9272 Y=-78.7794 Z=0
    g347: GeomPoint X=-7.42095 Y=-80.8542 Z=0
    g348: Circle CenterX=42.5666 CenterY=-53.4075 CenterZ=0 NormalX=0 NormalY=0 NormalZ=1 AngleXU=0 Radius=1
    g349: Circle CenterX=46.0728 CenterY=-51.4823 CenterZ=0 NormalX=0 NormalY=0 NormalZ=1 AngleXU=0 Radius=1
    g350: Circle CenterX=46.0728 CenterY=-47.4823 CenterZ=0 NormalX=0 NormalY=0 NormalZ=1 AngleXU=0 Radius=1
    g351: BSplineCurve PolesCount=3 KnotsCount=2 Degree=2 IsPeriodic=0
    g352: GeomPoint X=42.5666 Y=-53.4075 Z=0
    g353: GeomPoint X=46.0728 Y=-47.4823 Z=0
    g354: Circle CenterX=46.0728 CenterY=72.4095 CenterZ=0 NormalX=0 NormalY=0 NormalZ=1 AngleXU=0 Radius=1
    g355: Circle CenterX=46.0728 CenterY=76.4095 CenterZ=0 NormalX=0 NormalY=0 NormalZ=1 AngleXU=0 Radius=1
    g356: Circle CenterX=42.0728 CenterY=76.4095 CenterZ=0 NormalX=0 NormalY=0 NormalZ=1 AngleXU=0 Radius=1
    g357: BSplineCurve PolesCount=3 KnotsCount=2 Degree=2 IsPeriodic=0
    g358: GeomPoint X=46.0728 Y=72.4095 Z=0
    g359: GeomPoint X=42.0728 Y=76.4095 Z=0
    g360: Circle CenterX=-6.92718 CenterY=76.4095 CenterZ=0 NormalX=0 NormalY=0 NormalZ=1 AngleXU=0 Radius=1
    g361: Circle CenterX=-10.9272 CenterY=76.4095 CenterZ=0 NormalX=0 NormalY=0 NormalZ=1 AngleXU=0 Radius=1
    g362: Circle CenterX=-10.9272 CenterY=72.4095 CenterZ=0 NormalX=0 NormalY=0 NormalZ=1 AngleXU=0 Radius=1
    g363: BSplineCurve PolesCount=3 KnotsCount=2 Degree=2 IsPeriodic=0
    g364: GeomPoint X=-6.92718 Y=76.4095 Z=0
    g365: GeomPoint X=-10.9272 Y=72.4095 Z=0
    g366: LineSegment StartX=-10.9272 StartY=72.4095 StartZ=0 EndX=-10.9272 EndY=-78.7794 EndZ=0
    g367: LineSegment StartX=-7.42095 StartY=-80.8542 StartZ=0 EndX=42.5666 EndY=-53.4075 EndZ=0
    g368: LineSegment StartX=46.0728 StartY=-47.4823 StartZ=0 EndX=46.0728 EndY=72.4095 EndZ=0
    g369: LineSegment StartX=42.0728 StartY=76.4095 StartZ=0 EndX=-6.92719 EndY=76.4095 EndZ=0
    g370: LineSegment StartX=232.072 StartY=136.221 StartZ=0 EndX=232.072 EndY=-117.815 EndZ=0
    g371: LineSegment StartX=132.072 StartY=136.221 StartZ=0 EndX=132.072 EndY=-121.309 EndZ=0
    g372: LineSegment StartX=245.072 StartY=136.221 StartZ=0 EndX=245.072 EndY=-116.499 EndZ=0
    g373: LineSegment StartX=119.072 StartY=136.221 StartZ=0 EndX=119.072 EndY=-116.228 EndZ=0
    g374: LineSegment StartX=-42.9272 StartY=136.221 StartZ=0 EndX=407.073 EndY=136.221 EndZ=0
    g375: LineSegment StartX=232.072 StartY=136.221 StartZ=0 EndX=220.072 EndY=136.221 EndZ=0
    g376: LineSegment StartX=232.072 StartY=136.221 StartZ=0 EndX=232.072 EndY=124.221 EndZ=0
    g377: LineSegment StartX=220.072 StartY=136.221 StartZ=0 EndX=220.072 EndY=124.221 EndZ=0
    g378: LineSegment StartX=220.072 StartY=136.221 StartZ=0 EndX=226.072 EndY=136.221 EndZ=0
    g379: LineSegment StartX=220.072 StartY=136.221 StartZ=0 EndX=220.072 EndY=130.221 EndZ=0
    g380: LineSegment StartX=220.072 StartY=124.221 StartZ=0 EndX=226.072 EndY=124.221 EndZ=0
    g381: LineSegment StartX=232.072 StartY=124.221 StartZ=0 EndX=232.072 EndY=127.221 EndZ=0
    g382: LineSegment StartX=232.072 StartY=136.221 StartZ=0 EndX=232.072 EndY=133.221 EndZ=0
    g383-g387: Circle x5 (B-spline internal-alignment scaffolding for g388; pole/knot coordinates omitted)
    g388: BSplineCurve PolesCount=5 KnotsCount=3 Degree=3 IsPeriodic=0
    g389: GeomPoint X=232.072 Y=133.221 Z=0
    g390: GeomPoint X=223.072 Y=130.221 Z=0
    g391: GeomPoint X=232.072 Y=127.221 Z=0
    g392: LineSegment StartX=189.124 StartY=124.221 StartZ=0 EndX=302.073 EndY=124.221 EndZ=0
    g393: LineSegment StartX=132.072 StartY=136.221 StartZ=0 EndX=132.072 EndY=124.221 EndZ=0
    g394: LineSegment StartX=132.072 StartY=136.221 StartZ=0 EndX=144.072 EndY=136.221 EndZ=0
    g395: LineSegment StartX=144.072 StartY=136.221 StartZ=0 EndX=144.072 EndY=124.221 EndZ=0
    g396: LineSegment StartX=144.072 StartY=124.221 StartZ=0 EndX=138.072 EndY=124.221 EndZ=0
    g397: LineSegment StartX=144.072 StartY=136.221 StartZ=0 EndX=138.072 EndY=136.221 EndZ=0
    g398: LineSegment StartX=144.072 StartY=136.221 StartZ=0 EndX=144.072 EndY=130.221 EndZ=0
    g399: LineSegment StartX=132.072 StartY=136.221 StartZ=0 EndX=132.072 EndY=133.221 EndZ=0
    g400: LineSegment StartX=132.072 StartY=133.221 StartZ=0 EndX=132.072 EndY=127.221 EndZ=0
    g401-g405: Circle x5 (B-spline internal-alignment scaffolding for g406; pole/knot coordinates omitted)
    g406: BSplineCurve PolesCount=5 KnotsCount=3 Degree=3 IsPeriodic=0
    g407: GeomPoint X=132.072 Y=133.221 Z=0
    ... +2 more geometry lines
  constraints (696):
    c: Vertical(g0)
    c: Vertical(g1)
    c: Block(g1)
    c: Block(g0)
    c: Weight(g4) = 1
    c: Equal(g4,g5)
    c: Equal(g4,g6)
    c: InternalAlignment(g4,g7)
    c: InternalAlignment(g5,g7)
    c: InternalAlignment(g6,g7)
    c: InternalAlignment(g8,g7)
    c: InternalAlignment(g9,g7)
    c: Weight(g10) = 1
    c: Equal(g10,g11)
    c: Equal(g10,g12)
    c: InternalAlignment(g10,g13)
    c: InternalAlignment(g11,g13)
    c: InternalAlignment(g12,g13)
    c: InternalAlignment(g14,g13)
    c: InternalAlignment(g15,g13)
    c: Block(g13)
    c: Block(g7)
    c: Weight(g16) = 1
    c: Equal(g16,g17)
    c: Equal(g16,g18)
    c: InternalAlignment(g16,g19)
    c: InternalAlignment(g17,g19)
    c: InternalAlignment(g18,g19)
    c: InternalAlignment(g20,g19)
    c: InternalAlignment(g21,g19)
    c: Weight(g22) = 1
    c: Equal(g22,g23)
    c: Equal(g22,g24)
    c: InternalAlignment(g22,g25)
    c: InternalAlignment(g23,g25)
    c: InternalAlignment(g24,g25)
    c: InternalAlignment(g26,g25)
    c: InternalAlignment(g27,g25)
    c: Block(g25)
    c: Block(g19)
    c: Weight(g28) = 1
    c: Equal(g28,g29)
    c: Equal(g28,g30)
    c: InternalAlignment(g28,g31)
    c: InternalAlignment(g29,g31)
    c: InternalAlignment(g30,g31)
    c: InternalAlignment(g32,g31)
    c: InternalAlignment(g33,g31)
    c: Weight(g34) = 1
    c: Equal(g34,g35)
    c: Equal(g34,g36)
    c: InternalAlignment(g34,g37)
    c: InternalAlignment(g35,g37)
    c: InternalAlignment(g36,g37)
    c: InternalAlignment(g38,g37)
    c: InternalAlignment(g39,g37)
    c: Block(g31)
    c: Block(g37)
    c: Coincident(g40,g1)
    c: Coincident(g40,g0)
    c: Horizontal(g40)
    c: Distance(g40) = 450
    c: Weight(g41) = 1
    c: Equal(g41,g42)
    c: Equal(g41,g43)
    c: InternalAlignment(g41,g44)
    c: InternalAlignment(g42,g44)
    c: InternalAlignment(g43,g44)
    c: InternalAlignment(g45,g44)
    c: InternalAlignment(g46,g44)
    c: Block(g44)
    c: Weight(g47) = 1
    c: Equal(g47,g48)
    c: Equal(g47,g49)
    c: InternalAlignment(g47,g50)
    c: InternalAlignment(g48,g50)
    c: InternalAlignment(g49,g50)
    c: InternalAlignment(g51,g50)
    c: InternalAlignment(g52,g50)
    c: Block(g50)
    c: Weight(g53) = 1
    c: Equal(g53,g54)
    c: Equal(g53,g55)
    c: InternalAlignment(g53,g56)
    c: InternalAlignment(g54,g56)
    c: InternalAlignment(g55,g56)
    c: InternalAlignment(g57,g56)
    c: InternalAlignment(g58,g56)
    c: Block(g56)
    c: Weight(g59) = 1
    c: Equal(g59,g60)
    c: Equal(g59,g61)
    c: InternalAlignment(g59,g62)
    c: InternalAlignment(g60,g62)
    c: InternalAlignment(g61,g62)
    c: InternalAlignment(g63,g62)
    c: InternalAlignment(g64,g62)
    c: Block(g62)
    c: Weight(g65) = 1
    c: Equal(g65,g66)
    c: Equal(g65,g67)
    c: InternalAlignment(g65,g68)
    c: InternalAlignment(g66,g68)
    c: InternalAlignment(g67,g68)
    c: InternalAlignment(g69,g68)
    c: InternalAlignment(g70,g68)
    c: Weight(g71) = 1
    c: Equal(g71,g72)
    c: Equal(g71,g73)
    c: InternalAlignment(g71,g74)
    c: InternalAlignment(g72,g74)
    c: InternalAlignment(g73,g74)
    c: InternalAlignment(g75,g74)
    c: InternalAlignment(g76,g74)
    c: Block(g68)
    c: Block(g74)
    c: Coincident(g77,g68)
    c: Coincident(g77,g74)
    c: Vertical(g77)
    c: Coincident(g78,g68)
    c: Coincident(g78,g50)
    c: Coincident(g79,g50)
    c: Coincident(g79,g74)
    c: Weight(g80) = 1
    c: Equal(g80,g81)
    c: Equal(g80,g82)
    c: InternalAlignment(g80,g83)
    c: InternalAlignment(g81,g83)
    c: InternalAlignment(g82,g83)
    c: InternalAlignment(g84,g83)
    c: InternalAlignment(g85,g83)
    c: Weight(g86) = 1
    c: Equal(g86,g87)
    c: Equal(g86,g88)
    c: InternalAlignment(g86,g89)
    c: InternalAlignment(g87,g89)
    c: InternalAlignment(g88,g89)
    c: InternalAlignment(g90,g89)
    c: InternalAlignment(g91,g89)
    c: Block(g83)
    c: Block(g89)
    c: Coincident(g92,g83)
    c: Coincident(g92,g89)
    c: Vertical(g92)
    c: Coincident(g93,g83)
    c: Coincident(g93,g44)
    c: Coincident(g94,g44)
    c: Coincident(g94,g89)
    c: Weight(g95) = 1
    c: Equal(g95,g96)
    c: Equal(g95,g97)
    c: InternalAlignment(g95,g98)
    c: InternalAlignment(g96,g98)
    c: InternalAlignment(g97,g98)
    c: InternalAlignment(g99,g98)
    c: InternalAlignment(g100,g98)
    c: Weight(g101) = 1
    c: Equal(g101,g102)
    c: Equal(g101,g103)
    c: InternalAlignment(g101,g104)
    c: InternalAlignment(g102,g104)
    c: InternalAlignment(g103,g104)
    c: InternalAlignment(g105,g104)
    c: InternalAlignment(g106,g104)
    c: Block(g98)
    c: Block(g104)
    c: Coincident(g107,g98)
    c: Coincident(g107,g104)
    c: Vertical(g107)
    c: Coincident(g108,g104)
    c: Coincident(g108,g62)
    c: Coincident(g109,g62)
    c: Coincident(g109,g98)
    c: Weight(g110) = 1
    c: Equal(g110,g111)
    c: Equal(g110,g112)
    c: InternalAlignment(g110,g113)
    c: InternalAlignment(g111,g113)
    c: InternalAlignment(g112,g113)
    c: InternalAlignment(g114,g113)
    c: InternalAlignment(g115,g113)
    c: Weight(g116) = 1
    c: Equal(g116,g117)
    c: Equal(g116,g118)
    c: InternalAlignment(g116,g119)
    c: InternalAlignment(g117,g119)
    c: InternalAlignment(g118,g119)
    c: InternalAlignment(g120,g119)
    c: InternalAlignment(g121,g119)
    c: Block(g113)
    c: Block(g119)
    c: Coincident(g122,g113)
    c: Coincident(g122,g119)
    c: Vertical(g122)
    c: Coincident(g123,g119)
    c: Coincident(g123,g56)
    c: Coincident(g124,g56)
    c: Coincident(g124,g113)
    c: Weight(g125) = 1
    c: Equal(g125,g126)
    c: Equal(g125,g127)
    c: InternalAlignment(g125,g128)
    c: InternalAlignment(g126,g128)
    c: InternalAlignment(g127,g128)
    c: InternalAlignment(g129,g128)
    c: InternalAlignment(g130,g128)
    c: Weight(g131) = 1
    c: Equal(g131,g132)
    c: Equal(g131,g133)
    c: InternalAlignment(g131,g134)
    c: InternalAlignment(g132,g134)
    c: InternalAlignment(g133,g134)
    c: InternalAlignment(g135,g134)
    c: InternalAlignment(g136,g134)
    c: Weight(g137) = 1
    c: Equal(g137,g138)
    c: Equal(g137,g139)
    c: InternalAlignment(g137,g140)
    c: InternalAlignment(g138,g140)
    c: InternalAlignment(g139,g140)
    c: InternalAlignment(g141,g140)
    c: InternalAlignment(g142,g140)
    c: Weight(g143) = 1
    c: Equal(g143,g144)
    c: Equal(g143,g145)
    c: InternalAlignment(g143,g146)
    c: InternalAlignment(g144,g146)
    c: InternalAlignment(g145,g146)
    c: InternalAlignment(g147,g146)
    c: InternalAlignment(g148,g146)
    c: Block(g146)
    c: Block(g140)
    c: Block(g134)
    c: Block(g128)
    c: Coincident(g149,g25)
    c: Coincident(g149,g146)
    c: Coincident(g150,g146)
    c: Coincident(g150,g140)
    c: Horizontal(g150)
    c: Coincident(g151,g140)
    c: Coincident(g151,g25)
    c: Vertical(g151)
    c: Coincident(g152,g19)
    c: Coincident(g152,g134)
    c: Vertical(g152)
    c: Coincident(g153,g134)
    c: Coincident(g153,g128)
    c: Horizontal(g153)
    c: Coincident(g154,g128)
    c: Coincident(g154,g19)
    c: Weight(g155) = 1
    c: Equal(g155,g156)
    c: Equal(g155,g157)
    c: InternalAlignment(g155,g158)
    c: InternalAlignment(g156,g158)
    c: InternalAlignment(g157,g158)
    c: InternalAlignment(g159,g158)
    c: InternalAlignment(g160,g158)
    c: Weight(g161) = 1
    c: Equal(g161,g162)
    c: Equal(g161,g163)
    c: InternalAlignment(g161,g164)
    c: InternalAlignment(g162,g164)
    c: InternalAlignment(g163,g164)
    c: InternalAlignment(g165,g164)
    c: InternalAlignment(g166,g164)
    c: Weight(g167) = 1
    c: Equal(g167,g168)
    c: Equal(g167,g169)
    c: InternalAlignment(g167,g170)
    c: InternalAlignment(g168,g170)
    c: InternalAlignment(g169,g170)
    c: InternalAlignment(g171,g170)
    c: InternalAlignment(g172,g170)
    c: Weight(g173) = 1
    c: Equal(g173,g174)
    c: Equal(g173,g175)
    c: InternalAlignment(g173,g176)
    c: InternalAlignment(g174,g176)
    c: InternalAlignment(g175,g176)
    c: InternalAlignment(g177,g176)
    c: InternalAlignment(g178,g176)
    c: Block(g176)
    c: Block(g170)
    c: Block(g164)
    c: Block(g158)
    c: Coincident(g179,g170)
    c: Coincident(g179,g7)
    c: Vertical(g179)
    c: Coincident(g180,g13)
    c: Coincident(g180,g164)
    c: Vertical(g180)
    c: Coincident(g181,g158)
    c: Coincident(g181,g13)
    c: Coincident(g182,g7)
    c: Weight(g183) = 1
    c: Equal(g183,g184)
    c: Equal(g183,g185)
    c: InternalAlignment(g183,g186)
    c: InternalAlignment(g184,g186)
    c: InternalAlignment(g185,g186)
    c: InternalAlignment(g187,g186)
    c: InternalAlignment(g188,g186)
    c: Weight(g189) = 1
    c: Equal(g189,g190)
    c: Equal(g189,g191)
    c: InternalAlignment(g189,g192)
    c: InternalAlignment(g190,g192)
    c: InternalAlignment(g191,g192)
    c: InternalAlignment(g193,g192)
    c: InternalAlignment(g194,g192)
    c: Block(g192)
    c: Block(g186)
    c: Coincident(g195,g192)
    c: Coincident(g195,g31)
    c: Coincident(g196,g31)
    c: Coincident(g196,g186)
    c: Coincident(g197,g186)
    c: Coincident(g197,g192)
    c: Vertical(g197)
    c: Weight(g198) = 1
    c: Equal(g198,g199)
    c: Equal(g198,g200)
    c: InternalAlignment(g198,g201)
    c: InternalAlignment(g199,g201)
    c: InternalAlignment(g200,g201)
    c: InternalAlignment(g202,g201)
    c: InternalAlignment(g203,g201)
    c: Weight(g204) = 1
    c: Equal(g204,g205)
    c: Equal(g204,g206)
    c: InternalAlignment(g204,g207)
    c: InternalAlignment(g205,g207)
    c: InternalAlignment(g206,g207)
    c: InternalAlignment(g208,g207)
    c: InternalAlignment(g209,g207)
    c: Block(g207)
    c: Block(g201)
    c: Coincident(g210,g201)
    c: Coincident(g210,g37)
    c: Coincident(g211,g37)
    c: Coincident(g211,g207)
    c: Coincident(g212,g207)
    c: Coincident(g212,g201)
    c: Vertical(g212)
    c: Horizontal(g213)
    c: Block(g213)
    c: Vertical(g214)
    c: Block(g214)
    c: Block(g215)
    c: Weight(g216) = 1
    c: Equal(g216,g217)
    c: Equal(g216,g218)
    c: InternalAlignment(g216,g219)
    c: InternalAlignment(g217,g219)
    c: InternalAlignment(g218,g219)
    c: InternalAlignment(g220,g219)
    c: InternalAlignment(g221,g219)
    c: Weight(g222) = 1
    c: Equal(g222,g223)
    c: Equal(g222,g224)
    c: InternalAlignment(g222,g225)
    c: InternalAlignment(g223,g225)
    c: InternalAlignment(g224,g225)
    c: InternalAlignment(g226,g225)
    c: InternalAlignment(g227,g225)
    c: Weight(g228) = 1
    c: Equal(g228,g229)
    c: Equal(g228,g230)
    c: InternalAlignment(g228,g231)
    c: InternalAlignment(g229,g231)
    c: InternalAlignment(g230,g231)
    c: InternalAlignment(g232,g231)
    c: InternalAlignment(g233,g231)
    c: Weight(g234) = 1
    c: Equal(g234,g235)
    c: Equal(g234,g236)
    c: InternalAlignment(g234,g237)
    c: InternalAlignment(g235,g237)
    c: InternalAlignment(g236,g237)
    c: InternalAlignment(g238,g237)
    c: InternalAlignment(g239,g237)
    c: Block(g219)
    c: Block(g225)
    c: Block(g231)
    c: Block(g237)
    c: Coincident(g240,g225)
    c: Coincident(g240,g219)
    c: Horizontal(g240)
    c: Block(g182)
    c: Weight(g241) = 1
    c: Equal(g241,g242)
    c: Equal(g241,g243)
    c: InternalAlignment(g241,g244)
    c: InternalAlignment(g242,g244)
    c: InternalAlignment(g243,g244)
    c: InternalAlignment(g245,g244)
    c: InternalAlignment(g246,g244)
    c: Weight(g247) = 1
    c: Equal(g247,g248)
    c: Equal(g247,g249)
    c: InternalAlignment(g247,g250)
    c: InternalAlignment(g248,g250)
    c: InternalAlignment(g249,g250)
    c: InternalAlignment(g251,g250)
    c: InternalAlignment(g252,g250)
    c: Block(g244)
    c: Block(g250)
    c: Coincident(g253,g244)
    c: Coincident(g253,g250)
    c: Weight(g254) = 1
    c: Equal(g254,g255)
    c: Equal(g254,g256)
    c: InternalAlignment(g254,g257)
    c: InternalAlignment(g255,g257)
    c: InternalAlignment(g256,g257)
    c: InternalAlignment(g258,g257)
    c: InternalAlignment(g259,g257)
    c: Weight(g260) = 1
    c: Equal(g260,g261)
    c: Equal(g260,g262)
    c: InternalAlignment(g260,g263)
    c: InternalAlignment(g261,g263)
    c: InternalAlignment(g262,g263)
    c: InternalAlignment(g264,g263)
    c: InternalAlignment(g265,g263)
    c: Weight(g266) = 1
    c: Equal(g266,g267)
    c: Equal(g266,g268)
    c: InternalAlignment(g266,g269)
    c: InternalAlignment(g267,g269)
    c: InternalAlignment(g268,g269)
    c: InternalAlignment(g270,g269)
    c: InternalAlignment(g271,g269)
    c: Block(g269)
    c: Block(g263)
    c: Block(g257)
    c: Coincident(g272,g263)
    c: Coincident(g272,g257)
    c: Coincident(g273,g257)
    c: Coincident(g273,g269)
    c: Vertical(g273)
    c: Coincident(g274,g269)
    c: Coincident(g274,g263)
    c: Horizontal(g274)
    c: Weight(g275) = 1
    c: Equal(g275,g276)
    c: InternalAlignment(g275,g277)
    c: InternalAlignment(g276,g277)
    c: InternalAlignment(g278,g277)
    c: InternalAlignment(g279,g277)
    c: Weight(g280) = 1
    c: InternalAlignment(g281,g283)
    c: InternalAlignment(g282,g283)
    c: InternalAlignment(g284,g283)
    c: InternalAlignment(g285,g283)
    c: Weight(g286) = 1
    c: Equal(g286,g287)
    c: Equal(g286,g288)
    c: InternalAlignment(g286,g289)
    c: InternalAlignment(g287,g289)
    c: InternalAlignment(g288,g289)
    c: InternalAlignment(g290,g289)
    c: InternalAlignment(g291,g289)
    c: Equal(g292,g293)
    c: Equal(g292,g294)
    c: InternalAlignment(g292,g295)
    c: InternalAlignment(g293,g295)
    c: InternalAlignment(g294,g295)
    c: InternalAlignment(g296,g295)
    c: InternalAlignment(g297,g295)
    c: Block(g283)
    c: Block(g289)
    c: Block(g295)
    c: Block(g277)
    c: Coincident(g298,g277)
    c: Coincident(g298,g283)
    c: Horizontal(g298)
    c: Coincident(g299,g283)
    c: Coincident(g299,g289)
    c: Vertical(g299)
    c: Coincident(g300,g289)
    c: Coincident(g300,g295)
    c: Horizontal(g300)
    c: Coincident(g301,g295)
    c: Coincident(g301,g277)
    c: Weight(g302) = 1
    c: Equal(g302,g303)
    c: Equal(g302,g304)
    c: InternalAlignment(g302,g305)
    c: InternalAlignment(g303,g305)
    c: InternalAlignment(g304,g305)
    c: InternalAlignment(g306,g305)
    c: InternalAlignment(g307,g305)
    c: Weight(g308) = 1
    c: Equal(g308,g309)
    c: Equal(g308,g310)
    c: InternalAlignment(g308,g311)
    c: InternalAlignment(g309,g311)
    c: InternalAlignment(g310,g311)
    c: InternalAlignment(g312,g311)
    c: Weight(g314) = 1
    c: Equal(g314,g315)
    c: Equal(g314,g316)
    c: InternalAlignment(g314,g317)
    c: InternalAlignment(g315,g317)
    c: InternalAlignment(g316,g317)
    c: InternalAlignment(g318,g317)
    c: InternalAlignment(g319,g317)
    c: Block(g317)
    c: Block(g311)
    c: Block(g305)
    c: Coincident(g320,g317)
    c: Coincident(g320,g311)
    c: Horizontal(g320)
    c: Coincident(g321,g311)
    c: Coincident(g321,g305)
    c: Vertical(g321)
    c: Coincident(g322,g305)
    c: Coincident(g322,g317)
    c: InternalAlignment(g323,g324)
    c: InternalAlignment(g325,g324)
    c: InternalAlignment(g326,g324)
    c: Block(g324)
    c: Equal(g327,g328)
    c: Equal(g327,g329)
    c: InternalAlignment(g327,g330)
    c: InternalAlignment(g328,g330)
    c: InternalAlignment(g329,g330)
    c: InternalAlignment(g331,g330)
    c: InternalAlignment(g332,g330)
    c: Block(g330)
    c: Coincident(g333,g324)
    c: Horizontal(g333)
    c: Block(g333)
    c: Coincident(g334,g324)
    c: Coincident(g334,g250)
    c: Vertical(g334)
    c: Coincident(g335,g330)
    c: Coincident(g335,g244)
    c: Vertical(g335)
    c: Block(g336)
    c: Block(g2)
    c: Distance(g334) = 119.89
    c: Coincident(g337,g336)
    c: Coincident(g337,g2)
    c: Coincident(g338,g2)
    c: Coincident(g338,g336)
    c: Block(g3)
    c: Block(g339)
    c: Coincident(g340,g339)
    c: Coincident(g340,g3)
    c: Coincident(g341,g339)
    c: Coincident(g341,g3)
    c: Block(g341)
    c: Block(g340)
    c: Weight(g342) = 1
    c: Equal(g342,g343)
    c: Equal(g342,g344)
    c: InternalAlignment(g342,g345)
    c: InternalAlignment(g343,g345)
    c: InternalAlignment(g344,g345)
    c: InternalAlignment(g346,g345)
    c: InternalAlignment(g347,g345)
    c: Weight(g348) = 1
    c: Equal(g348,g349)
    c: Equal(g348,g350)
    c: InternalAlignment(g348,g351)
    c: InternalAlignment(g349,g351)
    c: InternalAlignment(g350,g351)
    c: InternalAlignment(g352,g351)
    c: InternalAlignment(g353,g351)
    c: Weight(g354) = 1
    c: Equal(g354,g355)
    c: Equal(g354,g356)
    c: InternalAlignment(g354,g357)
    c: InternalAlignment(g355,g357)
    c: InternalAlignment(g356,g357)
    c: InternalAlignment(g358,g357)
    c: InternalAlignment(g359,g357)
    c: Weight(g360) = 1
    c: Equal(g360,g361)
    c: Equal(g360,g362)
    c: InternalAlignment(g360,g363)
    c: InternalAlignment(g361,g363)
    c: InternalAlignment(g362,g363)
    c: InternalAlignment(g364,g363)
    c: InternalAlignment(g365,g363)
    c: Block(g363)
    c: Block(g357)
    c: Block(g351)
    c: Block(g345)
    c: Coincident(g366,g363)
    c: Coincident(g366,g345)
    c: Vertical(g366)
    c: Coincident(g367,g345)
    c: Coincident(g367,g351)
    c: Coincident(g368,g351)
    c: Coincident(g368,g357)
    c: Vertical(g368)
    c: Coincident(g369,g357)
    c: Coincident(g369,g363)
    c: Horizontal(g369)
    c: Vertical(g370)
    c: Vertical(g371)
    c: Vertical(g372)
    c: Vertical(g373)
    c: Coincident(g374,g0)
    c: Coincident(g374,g1)
    c: Horizontal(g374)
    c: Block(g374)
    c: Distance(g374) = 450
    c: Block(g372)
    c: Block(g370)
    c: Block(g371)
    c: Block(g373)
    c: Distance(g0) = 240
    c: Horizontal(g375)
    c: Distance(g375) = 12
    c: Coincident(g375,g370)
    c: Vertical(g376)
    c: Distance(g376) = 12
    c: Coincident(g376,g370)
    c: Coincident(g377,g375)
    c: Vertical(g377)
    c: Horizontal(g378)
    c: Vertical(g379)
    c: Distance(g379) = 6
    c: Coincident(g379,g375)
    c: Coincident(g378,g375)
    c: Block(g377)
    c: Coincident(g380,g377)
    c: Horizontal(g380)
    c: Distance(g380) = 6
    c: Vertical(g381)
    c: Distance(g381) = 3
    c: Vertical(g382)
    c: Distance(g382) = 3
    c: Coincident(g382,g370)
    c: Coincident(g376,g381)
    c: Coincident(g388,g382)
    c: Weight(g383) = 1
    c: Equal(g383,g384)
    c: Coincident(g384,g378)
    c: Equal(g383,g385)
    c: Coincident(g385,g379)
    c: Equal(g383,g386)
    c: Coincident(g386,g380)
    c: Equal(g383,g387)
    c: Coincident(g388,g381)
    c: InternalAlignment(g383-g387 -> g388) x5
    c: InternalAlignment(g389,g388)
    c: InternalAlignment(g390,g388)
    c: InternalAlignment(g391,g388)
    c: Coincident(g392,g164)
    c: Coincident(g392,g158)
    c: Horizontal(g392)
    c: Block(g388)
    c: Vertical(g393)
    c: Distance(g393) = 12
    c: Coincident(g393,g371)
    c: Horizontal(g394)
    c: Distance(g394) = 12
    c: Coincident(g394,g371)
    c: Coincident(g395,g394)
    c: Vertical(g395)
    c: Distance(g395) = 12
    c: Coincident(g396,g395)
    c: Horizontal(g396)
    c: Distance(g396) = 6
    c: Horizontal(g397)
    c: Distance(g397) = 6
    c: Coincident(g397,g394)
    c: Vertical(g398)
    c: Distance(g398) = 6
    c: Coincident(g398,g394)
    c: Vertical(g399)
    c: Distance(g399) = 3
    c: Coincident(g399,g371)
    c: Vertical(g400)
    c: Distance(g400) = 6
    c: Coincident(g400,g399)
    c: Coincident(g406,g399)
    c: Weight(g401) = 1
    c: Equal(g401,g402)
    c: Coincident(g402,g397)
    c: Equal(g401,g403)
    c: Coincident(g403,g398)
    c: Equal(g401,g404)
    c: Coincident(g404,g396)
    c: Equal(g401,g405)
    c: Coincident(g406,g400)
    c: InternalAlignment(g401-g405 -> g406) x5
    c: InternalAlignment(g407,g406)
    c: InternalAlignment(g408,g406)
    c: InternalAlignment(g409,g406)
FEATURE [Part::Extrusion] Extrude005
  Base = -> Sketch003
  Dir = (0,0,1)
  DirMode = 2
  FaceMakerClass = Part::FaceMakerBullseye
  LengthFwd = 24
  LengthRev = 0
  Solid = true
  Symmetric = false
